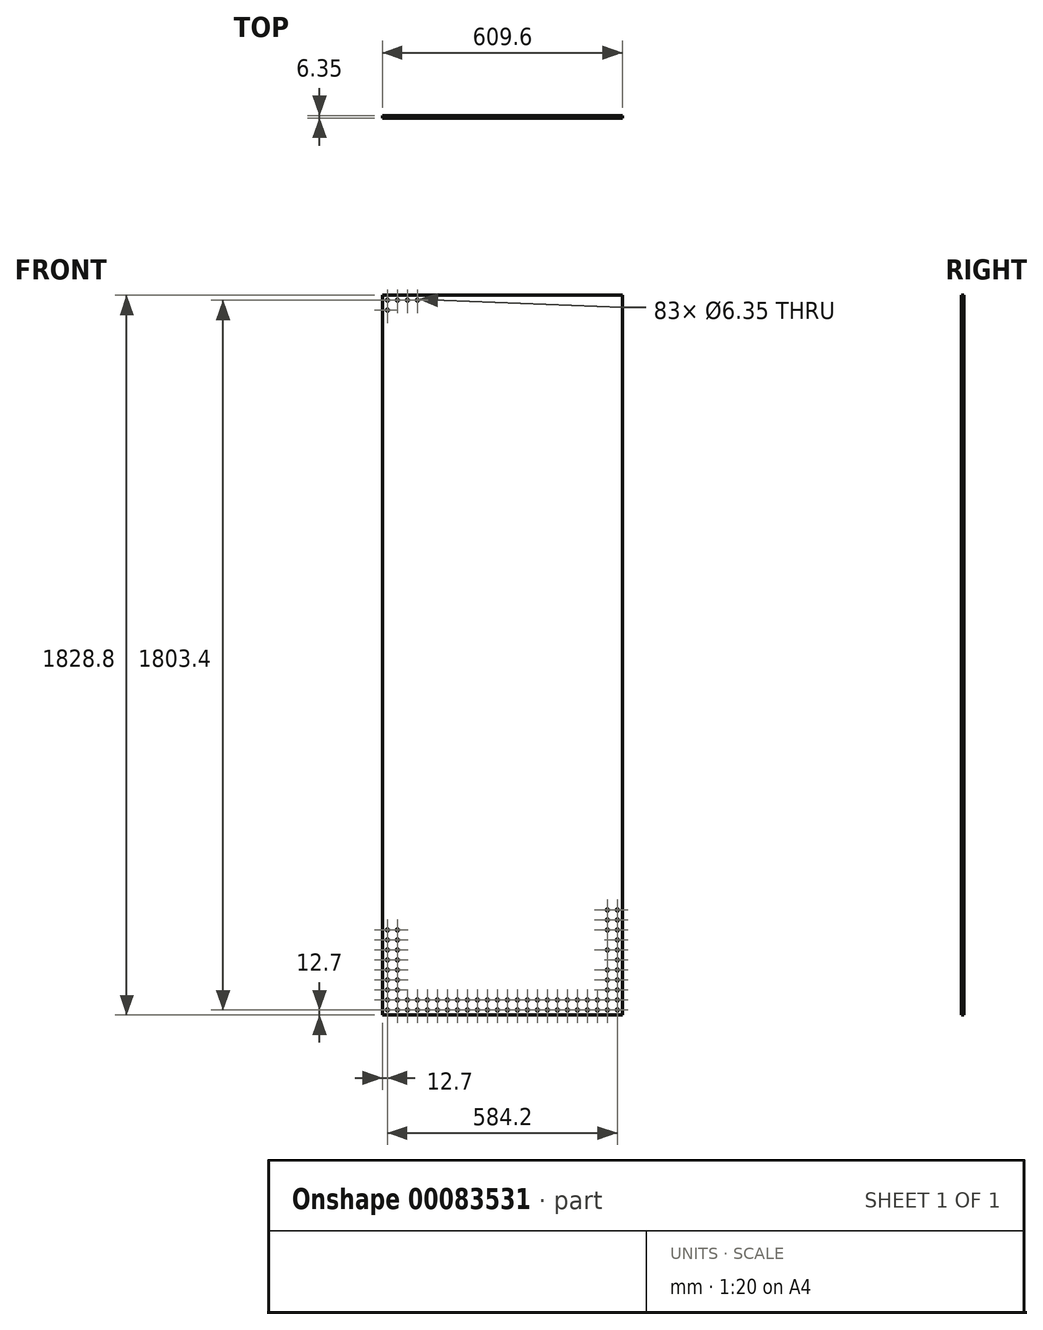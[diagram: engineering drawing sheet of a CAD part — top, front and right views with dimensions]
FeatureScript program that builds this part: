
annotation { "Feature Type Name" : "Feature", "Feature Type Description" : "" }
export const myFeature = defineFeature(function(context is Context, id is Id, definition is map)
    precondition{}
    {
        {
            var Q0;
            Q0=qCreatedBy(makeId("Front.planeOp"),FACE);
            var sketch = newSketch(context, id + "F0", { "sketchPlane" : qUnion([Q0])});
            skLineSegment(sketch, "E0.bottom", {"start": v(-304.8, 914.4) * mm, "end": v(304.8, 914.4) * mm});
            skLineSegment(sketch, "E0.top", {"start": v(-304.8, -914.4) * mm, "end": v(304.8, -914.4) * mm});
            skLineSegment(sketch, "E0.left", {"start": v(-304.8, 914.4) * mm, "end": v(-304.8, -914.4) * mm});
            skLineSegment(sketch, "E0.right", {"start": v(304.8, 914.4) * mm, "end": v(304.8, -914.4) * mm});
            skPoint(sketch, "E0.middle", {"position": v(0, 0) * mm});
            skPoint(sketch, "E1", {"position": v(-292.1, -901.7) * mm});
            skPoint(sketch, "E2.0.1.0", {"position": v(-292.1, -876.3) * mm});
            skPoint(sketch, "E2.0.2.0", {"position": v(-292.1, -850.9) * mm});
            skPoint(sketch, "E2.0.3.0", {"position": v(-292.1, -825.5) * mm});
            skPoint(sketch, "E2.0.4.0", {"position": v(-292.1, -800.1) * mm});
            skPoint(sketch, "E2.0.5.0", {"position": v(-292.1, -774.7) * mm});
            skPoint(sketch, "E2.0.6.0", {"position": v(-292.1, -749.3) * mm});
            skPoint(sketch, "E2.0.7.0", {"position": v(-292.1, -723.9) * mm});
            skPoint(sketch, "E2.0.8.0", {"position": v(-292.1, -698.5) * mm});
            skPoint(sketch, "E2.0.9.0", {"position": v(-292.1, -673.1) * mm});
            skPoint(sketch, "E2.0.10.0", {"position": v(-292.1, -647.7) * mm});
            skPoint(sketch, "E2.0.11.0", {"position": v(-292.1, -622.3) * mm});
            skPoint(sketch, "E2.0.12.0", {"position": v(-292.1, -596.9) * mm});
            skPoint(sketch, "E2.0.13.0", {"position": v(-292.1, -571.5) * mm});
            skPoint(sketch, "E2.0.14.0", {"position": v(-292.1, -546.1) * mm});
            skPoint(sketch, "E2.0.15.0", {"position": v(-292.1, -520.7) * mm});
            skPoint(sketch, "E2.0.16.0", {"position": v(-292.1, -495.3) * mm});
            skPoint(sketch, "E2.0.17.0", {"position": v(-292.1, -469.9) * mm});
            skPoint(sketch, "E2.0.18.0", {"position": v(-292.1, -444.5) * mm});
            skPoint(sketch, "E2.0.19.0", {"position": v(-292.1, -419.1) * mm});
            skPoint(sketch, "E2.0.20.0", {"position": v(-292.1, -393.7) * mm});
            skPoint(sketch, "E2.0.21.0", {"position": v(-292.1, -368.3) * mm});
            skPoint(sketch, "E2.0.22.0", {"position": v(-292.1, -342.9) * mm});
            skPoint(sketch, "E2.0.23.0", {"position": v(-292.1, -317.5) * mm});
            skPoint(sketch, "E2.0.24.0", {"position": v(-292.1, -292.1) * mm});
            skPoint(sketch, "E2.0.25.0", {"position": v(-292.1, -266.7) * mm});
            skPoint(sketch, "E2.0.26.0", {"position": v(-292.1, -241.3) * mm});
            skPoint(sketch, "E2.0.27.0", {"position": v(-292.1, -215.9) * mm});
            skPoint(sketch, "E2.0.28.0", {"position": v(-292.1, -190.5) * mm});
            skPoint(sketch, "E2.0.29.0", {"position": v(-292.1, -165.1) * mm});
            skPoint(sketch, "E2.0.30.0", {"position": v(-292.1, -139.7) * mm});
            skPoint(sketch, "E2.0.31.0", {"position": v(-292.1, -114.3) * mm});
            skPoint(sketch, "E2.0.32.0", {"position": v(-292.1, -88.9) * mm});
            skPoint(sketch, "E2.0.33.0", {"position": v(-292.1, -63.5) * mm});
            skPoint(sketch, "E2.0.34.0", {"position": v(-292.1, -38.1) * mm});
            skPoint(sketch, "E2.0.35.0", {"position": v(-292.1, -12.7) * mm});
            skPoint(sketch, "E2.0.36.0", {"position": v(-292.1, 12.7) * mm});
            skPoint(sketch, "E2.0.37.0", {"position": v(-292.1, 38.1) * mm});
            skPoint(sketch, "E2.0.38.0", {"position": v(-292.1, 63.5) * mm});
            skPoint(sketch, "E2.0.39.0", {"position": v(-292.1, 88.9) * mm});
            skPoint(sketch, "E2.0.40.0", {"position": v(-292.1, 114.3) * mm});
            skPoint(sketch, "E2.0.41.0", {"position": v(-292.1, 139.7) * mm});
            skPoint(sketch, "E2.0.42.0", {"position": v(-292.1, 165.1) * mm});
            skPoint(sketch, "E2.0.43.0", {"position": v(-292.1, 190.5) * mm});
            skPoint(sketch, "E2.0.44.0", {"position": v(-292.1, 215.9) * mm});
            skPoint(sketch, "E2.0.45.0", {"position": v(-292.1, 241.3) * mm});
            skPoint(sketch, "E2.0.46.0", {"position": v(-292.1, 266.7) * mm});
            skPoint(sketch, "E2.0.47.0", {"position": v(-292.1, 292.1) * mm});
            skPoint(sketch, "E2.0.48.0", {"position": v(-292.1, 317.5) * mm});
            skPoint(sketch, "E2.0.49.0", {"position": v(-292.1, 342.9) * mm});
            skPoint(sketch, "E2.0.50.0", {"position": v(-292.1, 368.3) * mm});
            skPoint(sketch, "E2.0.51.0", {"position": v(-292.1, 393.7) * mm});
            skPoint(sketch, "E2.0.52.0", {"position": v(-292.1, 419.1) * mm});
            skPoint(sketch, "E2.0.53.0", {"position": v(-292.1, 444.5) * mm});
            skPoint(sketch, "E2.0.54.0", {"position": v(-292.1, 469.9) * mm});
            skPoint(sketch, "E2.0.55.0", {"position": v(-292.1, 495.3) * mm});
            skPoint(sketch, "E2.0.56.0", {"position": v(-292.1, 520.7) * mm});
            skPoint(sketch, "E2.0.57.0", {"position": v(-292.1, 546.1) * mm});
            skPoint(sketch, "E2.0.58.0", {"position": v(-292.1, 571.5) * mm});
            skPoint(sketch, "E2.0.59.0", {"position": v(-292.1, 596.9) * mm});
            skPoint(sketch, "E2.0.60.0", {"position": v(-292.1, 622.3) * mm});
            skPoint(sketch, "E2.0.61.0", {"position": v(-292.1, 647.7) * mm});
            skPoint(sketch, "E2.0.62.0", {"position": v(-292.1, 673.1) * mm});
            skPoint(sketch, "E2.0.63.0", {"position": v(-292.1, 698.5) * mm});
            skPoint(sketch, "E2.0.64.0", {"position": v(-292.1, 723.9) * mm});
            skPoint(sketch, "E2.0.65.0", {"position": v(-292.1, 749.3) * mm});
            skPoint(sketch, "E2.0.66.0", {"position": v(-292.1, 774.7) * mm});
            skPoint(sketch, "E2.0.67.0", {"position": v(-292.1, 800.1) * mm});
            skPoint(sketch, "E2.0.68.0", {"position": v(-292.1, 825.5) * mm});
            skPoint(sketch, "E2.0.69.0", {"position": v(-292.1, 850.9) * mm});
            skPoint(sketch, "E2.0.70.0", {"position": v(-292.1, 876.3) * mm});
            skPoint(sketch, "E2.0.71.0", {"position": v(-292.1, 901.7) * mm});
            skPoint(sketch, "E2.1.0.0", {"position": v(-266.7, -901.7) * mm});
            skPoint(sketch, "E2.1.1.0", {"position": v(-266.7, -876.3) * mm});
            skPoint(sketch, "E2.1.2.0", {"position": v(-266.7, -850.9) * mm});
            skPoint(sketch, "E2.1.3.0", {"position": v(-266.7, -825.5) * mm});
            skPoint(sketch, "E2.1.4.0", {"position": v(-266.7, -800.1) * mm});
            skPoint(sketch, "E2.1.5.0", {"position": v(-266.7, -774.7) * mm});
            skPoint(sketch, "E2.1.6.0", {"position": v(-266.7, -749.3) * mm});
            skPoint(sketch, "E2.1.7.0", {"position": v(-266.7, -723.9) * mm});
            skPoint(sketch, "E2.1.8.0", {"position": v(-266.7, -698.5) * mm});
            skPoint(sketch, "E2.1.9.0", {"position": v(-266.7, -673.1) * mm});
            skPoint(sketch, "E2.1.10.0", {"position": v(-266.7, -647.7) * mm});
            skPoint(sketch, "E2.1.11.0", {"position": v(-266.7, -622.3) * mm});
            skPoint(sketch, "E2.1.12.0", {"position": v(-266.7, -596.9) * mm});
            skPoint(sketch, "E2.1.13.0", {"position": v(-266.7, -571.5) * mm});
            skPoint(sketch, "E2.1.14.0", {"position": v(-266.7, -546.1) * mm});
            skPoint(sketch, "E2.1.15.0", {"position": v(-266.7, -520.7) * mm});
            skPoint(sketch, "E2.1.16.0", {"position": v(-266.7, -495.3) * mm});
            skPoint(sketch, "E2.1.17.0", {"position": v(-266.7, -469.9) * mm});
            skPoint(sketch, "E2.1.18.0", {"position": v(-266.7, -444.5) * mm});
            skPoint(sketch, "E2.1.19.0", {"position": v(-266.7, -419.1) * mm});
            skPoint(sketch, "E2.1.20.0", {"position": v(-266.7, -393.7) * mm});
            skPoint(sketch, "E2.1.21.0", {"position": v(-266.7, -368.3) * mm});
            skPoint(sketch, "E2.1.22.0", {"position": v(-266.7, -342.9) * mm});
            skPoint(sketch, "E2.1.23.0", {"position": v(-266.7, -317.5) * mm});
            skPoint(sketch, "E2.1.24.0", {"position": v(-266.7, -292.1) * mm});
            skPoint(sketch, "E2.1.25.0", {"position": v(-266.7, -266.7) * mm});
            skPoint(sketch, "E2.1.26.0", {"position": v(-266.7, -241.3) * mm});
            skPoint(sketch, "E2.1.27.0", {"position": v(-266.7, -215.9) * mm});
            skPoint(sketch, "E2.1.28.0", {"position": v(-266.7, -190.5) * mm});
            skPoint(sketch, "E2.1.29.0", {"position": v(-266.7, -165.1) * mm});
            skPoint(sketch, "E2.1.30.0", {"position": v(-266.7, -139.7) * mm});
            skPoint(sketch, "E2.1.31.0", {"position": v(-266.7, -114.3) * mm});
            skPoint(sketch, "E2.1.32.0", {"position": v(-266.7, -88.9) * mm});
            skPoint(sketch, "E2.1.33.0", {"position": v(-266.7, -63.5) * mm});
            skPoint(sketch, "E2.1.34.0", {"position": v(-266.7, -38.1) * mm});
            skPoint(sketch, "E2.1.35.0", {"position": v(-266.7, -12.7) * mm});
            skPoint(sketch, "E2.1.36.0", {"position": v(-266.7, 12.7) * mm});
            skPoint(sketch, "E2.1.37.0", {"position": v(-266.7, 38.1) * mm});
            skPoint(sketch, "E2.1.38.0", {"position": v(-266.7, 63.5) * mm});
            skPoint(sketch, "E2.1.39.0", {"position": v(-266.7, 88.9) * mm});
            skPoint(sketch, "E2.1.40.0", {"position": v(-266.7, 114.3) * mm});
            skPoint(sketch, "E2.1.41.0", {"position": v(-266.7, 139.7) * mm});
            skPoint(sketch, "E2.1.42.0", {"position": v(-266.7, 165.1) * mm});
            skPoint(sketch, "E2.1.43.0", {"position": v(-266.7, 190.5) * mm});
            skPoint(sketch, "E2.1.44.0", {"position": v(-266.7, 215.9) * mm});
            skPoint(sketch, "E2.1.45.0", {"position": v(-266.7, 241.3) * mm});
            skPoint(sketch, "E2.1.46.0", {"position": v(-266.7, 266.7) * mm});
            skPoint(sketch, "E2.1.47.0", {"position": v(-266.7, 292.1) * mm});
            skPoint(sketch, "E2.1.48.0", {"position": v(-266.7, 317.5) * mm});
            skPoint(sketch, "E2.1.49.0", {"position": v(-266.7, 342.9) * mm});
            skPoint(sketch, "E2.1.50.0", {"position": v(-266.7, 368.3) * mm});
            skPoint(sketch, "E2.1.51.0", {"position": v(-266.7, 393.7) * mm});
            skPoint(sketch, "E2.1.52.0", {"position": v(-266.7, 419.1) * mm});
            skPoint(sketch, "E2.1.53.0", {"position": v(-266.7, 444.5) * mm});
            skPoint(sketch, "E2.1.54.0", {"position": v(-266.7, 469.9) * mm});
            skPoint(sketch, "E2.1.55.0", {"position": v(-266.7, 495.3) * mm});
            skPoint(sketch, "E2.1.56.0", {"position": v(-266.7, 520.7) * mm});
            skPoint(sketch, "E2.1.57.0", {"position": v(-266.7, 546.1) * mm});
            skPoint(sketch, "E2.1.58.0", {"position": v(-266.7, 571.5) * mm});
            skPoint(sketch, "E2.1.59.0", {"position": v(-266.7, 596.9) * mm});
            skPoint(sketch, "E2.1.60.0", {"position": v(-266.7, 622.3) * mm});
            skPoint(sketch, "E2.1.61.0", {"position": v(-266.7, 647.7) * mm});
            skPoint(sketch, "E2.1.62.0", {"position": v(-266.7, 673.1) * mm});
            skPoint(sketch, "E2.1.63.0", {"position": v(-266.7, 698.5) * mm});
            skPoint(sketch, "E2.1.64.0", {"position": v(-266.7, 723.9) * mm});
            skPoint(sketch, "E2.1.65.0", {"position": v(-266.7, 749.3) * mm});
            skPoint(sketch, "E2.1.66.0", {"position": v(-266.7, 774.7) * mm});
            skPoint(sketch, "E2.1.67.0", {"position": v(-266.7, 800.1) * mm});
            skPoint(sketch, "E2.1.68.0", {"position": v(-266.7, 825.5) * mm});
            skPoint(sketch, "E2.1.69.0", {"position": v(-266.7, 850.9) * mm});
            skPoint(sketch, "E2.1.70.0", {"position": v(-266.7, 876.3) * mm});
            skPoint(sketch, "E2.1.71.0", {"position": v(-266.7, 901.7) * mm});
            skPoint(sketch, "E2.2.0.0", {"position": v(-241.3, -901.7) * mm});
            skPoint(sketch, "E2.2.1.0", {"position": v(-241.3, -876.3) * mm});
            skPoint(sketch, "E2.2.2.0", {"position": v(-241.3, -850.9) * mm});
            skPoint(sketch, "E2.2.3.0", {"position": v(-241.3, -825.5) * mm});
            skPoint(sketch, "E2.2.4.0", {"position": v(-241.3, -800.1) * mm});
            skPoint(sketch, "E2.2.5.0", {"position": v(-241.3, -774.7) * mm});
            skPoint(sketch, "E2.2.6.0", {"position": v(-241.3, -749.3) * mm});
            skPoint(sketch, "E2.2.7.0", {"position": v(-241.3, -723.9) * mm});
            skPoint(sketch, "E2.2.8.0", {"position": v(-241.3, -698.5) * mm});
            skPoint(sketch, "E2.2.9.0", {"position": v(-241.3, -673.1) * mm});
            skPoint(sketch, "E2.2.10.0", {"position": v(-241.3, -647.7) * mm});
            skPoint(sketch, "E2.2.11.0", {"position": v(-241.3, -622.3) * mm});
            skPoint(sketch, "E2.2.12.0", {"position": v(-241.3, -596.9) * mm});
            skPoint(sketch, "E2.2.13.0", {"position": v(-241.3, -571.5) * mm});
            skPoint(sketch, "E2.2.14.0", {"position": v(-241.3, -546.1) * mm});
            skPoint(sketch, "E2.2.15.0", {"position": v(-241.3, -520.7) * mm});
            skPoint(sketch, "E2.2.16.0", {"position": v(-241.3, -495.3) * mm});
            skPoint(sketch, "E2.2.17.0", {"position": v(-241.3, -469.9) * mm});
            skPoint(sketch, "E2.2.18.0", {"position": v(-241.3, -444.5) * mm});
            skPoint(sketch, "E2.2.19.0", {"position": v(-241.3, -419.1) * mm});
            skPoint(sketch, "E2.2.20.0", {"position": v(-241.3, -393.7) * mm});
            skPoint(sketch, "E2.2.21.0", {"position": v(-241.3, -368.3) * mm});
            skPoint(sketch, "E2.2.22.0", {"position": v(-241.3, -342.9) * mm});
            skPoint(sketch, "E2.2.23.0", {"position": v(-241.3, -317.5) * mm});
            skPoint(sketch, "E2.2.24.0", {"position": v(-241.3, -292.1) * mm});
            skPoint(sketch, "E2.2.25.0", {"position": v(-241.3, -266.7) * mm});
            skPoint(sketch, "E2.2.26.0", {"position": v(-241.3, -241.3) * mm});
            skPoint(sketch, "E2.2.27.0", {"position": v(-241.3, -215.9) * mm});
            skPoint(sketch, "E2.2.28.0", {"position": v(-241.3, -190.5) * mm});
            skPoint(sketch, "E2.2.29.0", {"position": v(-241.3, -165.1) * mm});
            skPoint(sketch, "E2.2.30.0", {"position": v(-241.3, -139.7) * mm});
            skPoint(sketch, "E2.2.31.0", {"position": v(-241.3, -114.3) * mm});
            skPoint(sketch, "E2.2.32.0", {"position": v(-241.3, -88.9) * mm});
            skPoint(sketch, "E2.2.33.0", {"position": v(-241.3, -63.5) * mm});
            skPoint(sketch, "E2.2.34.0", {"position": v(-241.3, -38.1) * mm});
            skPoint(sketch, "E2.2.35.0", {"position": v(-241.3, -12.7) * mm});
            skPoint(sketch, "E2.2.36.0", {"position": v(-241.3, 12.7) * mm});
            skPoint(sketch, "E2.2.37.0", {"position": v(-241.3, 38.1) * mm});
            skPoint(sketch, "E2.2.38.0", {"position": v(-241.3, 63.5) * mm});
            skPoint(sketch, "E2.2.39.0", {"position": v(-241.3, 88.9) * mm});
            skPoint(sketch, "E2.2.40.0", {"position": v(-241.3, 114.3) * mm});
            skPoint(sketch, "E2.2.41.0", {"position": v(-241.3, 139.7) * mm});
            skPoint(sketch, "E2.2.42.0", {"position": v(-241.3, 165.1) * mm});
            skPoint(sketch, "E2.2.43.0", {"position": v(-241.3, 190.5) * mm});
            skPoint(sketch, "E2.2.44.0", {"position": v(-241.3, 215.9) * mm});
            skPoint(sketch, "E2.2.45.0", {"position": v(-241.3, 241.3) * mm});
            skPoint(sketch, "E2.2.46.0", {"position": v(-241.3, 266.7) * mm});
            skPoint(sketch, "E2.2.47.0", {"position": v(-241.3, 292.1) * mm});
            skPoint(sketch, "E2.2.48.0", {"position": v(-241.3, 317.5) * mm});
            skPoint(sketch, "E2.2.49.0", {"position": v(-241.3, 342.9) * mm});
            skPoint(sketch, "E2.2.50.0", {"position": v(-241.3, 368.3) * mm});
            skPoint(sketch, "E2.2.51.0", {"position": v(-241.3, 393.7) * mm});
            skPoint(sketch, "E2.2.52.0", {"position": v(-241.3, 419.1) * mm});
            skPoint(sketch, "E2.2.53.0", {"position": v(-241.3, 444.5) * mm});
            skPoint(sketch, "E2.2.54.0", {"position": v(-241.3, 469.9) * mm});
            skPoint(sketch, "E2.2.55.0", {"position": v(-241.3, 495.3) * mm});
            skPoint(sketch, "E2.2.56.0", {"position": v(-241.3, 520.7) * mm});
            skPoint(sketch, "E2.2.57.0", {"position": v(-241.3, 546.1) * mm});
            skPoint(sketch, "E2.2.58.0", {"position": v(-241.3, 571.5) * mm});
            skPoint(sketch, "E2.2.59.0", {"position": v(-241.3, 596.9) * mm});
            skPoint(sketch, "E2.2.60.0", {"position": v(-241.3, 622.3) * mm});
            skPoint(sketch, "E2.2.61.0", {"position": v(-241.3, 647.7) * mm});
            skPoint(sketch, "E2.2.62.0", {"position": v(-241.3, 673.1) * mm});
            skPoint(sketch, "E2.2.63.0", {"position": v(-241.3, 698.5) * mm});
            skPoint(sketch, "E2.2.64.0", {"position": v(-241.3, 723.9) * mm});
            skPoint(sketch, "E2.2.65.0", {"position": v(-241.3, 749.3) * mm});
            skPoint(sketch, "E2.2.66.0", {"position": v(-241.3, 774.7) * mm});
            skPoint(sketch, "E2.2.67.0", {"position": v(-241.3, 800.1) * mm});
            skPoint(sketch, "E2.2.68.0", {"position": v(-241.3, 825.5) * mm});
            skPoint(sketch, "E2.2.69.0", {"position": v(-241.3, 850.9) * mm});
            skPoint(sketch, "E2.2.70.0", {"position": v(-241.3, 876.3) * mm});
            skPoint(sketch, "E2.2.71.0", {"position": v(-241.3, 901.7) * mm});
            skPoint(sketch, "E2.3.0.0", {"position": v(-215.9, -901.7) * mm});
            skPoint(sketch, "E2.3.1.0", {"position": v(-215.9, -876.3) * mm});
            skPoint(sketch, "E2.3.2.0", {"position": v(-215.9, -850.9) * mm});
            skPoint(sketch, "E2.3.3.0", {"position": v(-215.9, -825.5) * mm});
            skPoint(sketch, "E2.3.4.0", {"position": v(-215.9, -800.1) * mm});
            skPoint(sketch, "E2.3.5.0", {"position": v(-215.9, -774.7) * mm});
            skPoint(sketch, "E2.3.6.0", {"position": v(-215.9, -749.3) * mm});
            skPoint(sketch, "E2.3.7.0", {"position": v(-215.9, -723.9) * mm});
            skPoint(sketch, "E2.3.8.0", {"position": v(-215.9, -698.5) * mm});
            skPoint(sketch, "E2.3.9.0", {"position": v(-215.9, -673.1) * mm});
            skPoint(sketch, "E2.3.10.0", {"position": v(-215.9, -647.7) * mm});
            skPoint(sketch, "E2.3.11.0", {"position": v(-215.9, -622.3) * mm});
            skPoint(sketch, "E2.3.12.0", {"position": v(-215.9, -596.9) * mm});
            skPoint(sketch, "E2.3.13.0", {"position": v(-215.9, -571.5) * mm});
            skPoint(sketch, "E2.3.14.0", {"position": v(-215.9, -546.1) * mm});
            skPoint(sketch, "E2.3.15.0", {"position": v(-215.9, -520.7) * mm});
            skPoint(sketch, "E2.3.16.0", {"position": v(-215.9, -495.3) * mm});
            skPoint(sketch, "E2.3.17.0", {"position": v(-215.9, -469.9) * mm});
            skPoint(sketch, "E2.3.18.0", {"position": v(-215.9, -444.5) * mm});
            skPoint(sketch, "E2.3.19.0", {"position": v(-215.9, -419.1) * mm});
            skPoint(sketch, "E2.3.20.0", {"position": v(-215.9, -393.7) * mm});
            skPoint(sketch, "E2.3.21.0", {"position": v(-215.9, -368.3) * mm});
            skPoint(sketch, "E2.3.22.0", {"position": v(-215.9, -342.9) * mm});
            skPoint(sketch, "E2.3.23.0", {"position": v(-215.9, -317.5) * mm});
            skPoint(sketch, "E2.3.24.0", {"position": v(-215.9, -292.1) * mm});
            skPoint(sketch, "E2.3.25.0", {"position": v(-215.9, -266.7) * mm});
            skPoint(sketch, "E2.3.26.0", {"position": v(-215.9, -241.3) * mm});
            skPoint(sketch, "E2.3.27.0", {"position": v(-215.9, -215.9) * mm});
            skPoint(sketch, "E2.3.28.0", {"position": v(-215.9, -190.5) * mm});
            skPoint(sketch, "E2.3.29.0", {"position": v(-215.9, -165.1) * mm});
            skPoint(sketch, "E2.3.30.0", {"position": v(-215.9, -139.7) * mm});
            skPoint(sketch, "E2.3.31.0", {"position": v(-215.9, -114.3) * mm});
            skPoint(sketch, "E2.3.32.0", {"position": v(-215.9, -88.9) * mm});
            skPoint(sketch, "E2.3.33.0", {"position": v(-215.9, -63.5) * mm});
            skPoint(sketch, "E2.3.34.0", {"position": v(-215.9, -38.1) * mm});
            skPoint(sketch, "E2.3.35.0", {"position": v(-215.9, -12.7) * mm});
            skPoint(sketch, "E2.3.36.0", {"position": v(-215.9, 12.7) * mm});
            skPoint(sketch, "E2.3.37.0", {"position": v(-215.9, 38.1) * mm});
            skPoint(sketch, "E2.3.38.0", {"position": v(-215.9, 63.5) * mm});
            skPoint(sketch, "E2.3.39.0", {"position": v(-215.9, 88.9) * mm});
            skPoint(sketch, "E2.3.40.0", {"position": v(-215.9, 114.3) * mm});
            skPoint(sketch, "E2.3.41.0", {"position": v(-215.9, 139.7) * mm});
            skPoint(sketch, "E2.3.42.0", {"position": v(-215.9, 165.1) * mm});
            skPoint(sketch, "E2.3.43.0", {"position": v(-215.9, 190.5) * mm});
            skPoint(sketch, "E2.3.44.0", {"position": v(-215.9, 215.9) * mm});
            skPoint(sketch, "E2.3.45.0", {"position": v(-215.9, 241.3) * mm});
            skPoint(sketch, "E2.3.46.0", {"position": v(-215.9, 266.7) * mm});
            skPoint(sketch, "E2.3.47.0", {"position": v(-215.9, 292.1) * mm});
            skPoint(sketch, "E2.3.48.0", {"position": v(-215.9, 317.5) * mm});
            skPoint(sketch, "E2.3.49.0", {"position": v(-215.9, 342.9) * mm});
            skPoint(sketch, "E2.3.50.0", {"position": v(-215.9, 368.3) * mm});
            skPoint(sketch, "E2.3.51.0", {"position": v(-215.9, 393.7) * mm});
            skPoint(sketch, "E2.3.52.0", {"position": v(-215.9, 419.1) * mm});
            skPoint(sketch, "E2.3.53.0", {"position": v(-215.9, 444.5) * mm});
            skPoint(sketch, "E2.3.54.0", {"position": v(-215.9, 469.9) * mm});
            skPoint(sketch, "E2.3.55.0", {"position": v(-215.9, 495.3) * mm});
            skPoint(sketch, "E2.3.56.0", {"position": v(-215.9, 520.7) * mm});
            skPoint(sketch, "E2.3.57.0", {"position": v(-215.9, 546.1) * mm});
            skPoint(sketch, "E2.3.58.0", {"position": v(-215.9, 571.5) * mm});
            skPoint(sketch, "E2.3.59.0", {"position": v(-215.9, 596.9) * mm});
            skPoint(sketch, "E2.3.60.0", {"position": v(-215.9, 622.3) * mm});
            skPoint(sketch, "E2.3.61.0", {"position": v(-215.9, 647.7) * mm});
            skPoint(sketch, "E2.3.62.0", {"position": v(-215.9, 673.1) * mm});
            skPoint(sketch, "E2.3.63.0", {"position": v(-215.9, 698.5) * mm});
            skPoint(sketch, "E2.3.64.0", {"position": v(-215.9, 723.9) * mm});
            skPoint(sketch, "E2.3.65.0", {"position": v(-215.9, 749.3) * mm});
            skPoint(sketch, "E2.3.66.0", {"position": v(-215.9, 774.7) * mm});
            skPoint(sketch, "E2.3.67.0", {"position": v(-215.9, 800.1) * mm});
            skPoint(sketch, "E2.3.68.0", {"position": v(-215.9, 825.5) * mm});
            skPoint(sketch, "E2.3.69.0", {"position": v(-215.9, 850.9) * mm});
            skPoint(sketch, "E2.3.70.0", {"position": v(-215.9, 876.3) * mm});
            skPoint(sketch, "E2.3.71.0", {"position": v(-215.9, 901.7) * mm});
            skPoint(sketch, "E2.4.0.0", {"position": v(-190.5, -901.7) * mm});
            skPoint(sketch, "E2.4.1.0", {"position": v(-190.5, -876.3) * mm});
            skPoint(sketch, "E2.4.2.0", {"position": v(-190.5, -850.9) * mm});
            skPoint(sketch, "E2.4.3.0", {"position": v(-190.5, -825.5) * mm});
            skPoint(sketch, "E2.4.4.0", {"position": v(-190.5, -800.1) * mm});
            skPoint(sketch, "E2.4.5.0", {"position": v(-190.5, -774.7) * mm});
            skPoint(sketch, "E2.4.6.0", {"position": v(-190.5, -749.3) * mm});
            skPoint(sketch, "E2.4.7.0", {"position": v(-190.5, -723.9) * mm});
            skPoint(sketch, "E2.4.8.0", {"position": v(-190.5, -698.5) * mm});
            skPoint(sketch, "E2.4.9.0", {"position": v(-190.5, -673.1) * mm});
            skPoint(sketch, "E2.4.10.0", {"position": v(-190.5, -647.7) * mm});
            skPoint(sketch, "E2.4.11.0", {"position": v(-190.5, -622.3) * mm});
            skPoint(sketch, "E2.4.12.0", {"position": v(-190.5, -596.9) * mm});
            skPoint(sketch, "E2.4.13.0", {"position": v(-190.5, -571.5) * mm});
            skPoint(sketch, "E2.4.14.0", {"position": v(-190.5, -546.1) * mm});
            skPoint(sketch, "E2.4.15.0", {"position": v(-190.5, -520.7) * mm});
            skPoint(sketch, "E2.4.16.0", {"position": v(-190.5, -495.3) * mm});
            skPoint(sketch, "E2.4.17.0", {"position": v(-190.5, -469.9) * mm});
            skPoint(sketch, "E2.4.18.0", {"position": v(-190.5, -444.5) * mm});
            skPoint(sketch, "E2.4.19.0", {"position": v(-190.5, -419.1) * mm});
            skPoint(sketch, "E2.4.20.0", {"position": v(-190.5, -393.7) * mm});
            skPoint(sketch, "E2.4.21.0", {"position": v(-190.5, -368.3) * mm});
            skPoint(sketch, "E2.4.22.0", {"position": v(-190.5, -342.9) * mm});
            skPoint(sketch, "E2.4.23.0", {"position": v(-190.5, -317.5) * mm});
            skPoint(sketch, "E2.4.24.0", {"position": v(-190.5, -292.1) * mm});
            skPoint(sketch, "E2.4.25.0", {"position": v(-190.5, -266.7) * mm});
            skPoint(sketch, "E2.4.26.0", {"position": v(-190.5, -241.3) * mm});
            skPoint(sketch, "E2.4.27.0", {"position": v(-190.5, -215.9) * mm});
            skPoint(sketch, "E2.4.28.0", {"position": v(-190.5, -190.5) * mm});
            skPoint(sketch, "E2.4.29.0", {"position": v(-190.5, -165.1) * mm});
            skPoint(sketch, "E2.4.30.0", {"position": v(-190.5, -139.7) * mm});
            skPoint(sketch, "E2.4.31.0", {"position": v(-190.5, -114.3) * mm});
            skPoint(sketch, "E2.4.32.0", {"position": v(-190.5, -88.9) * mm});
            skPoint(sketch, "E2.4.33.0", {"position": v(-190.5, -63.5) * mm});
            skPoint(sketch, "E2.4.34.0", {"position": v(-190.5, -38.1) * mm});
            skPoint(sketch, "E2.4.35.0", {"position": v(-190.5, -12.7) * mm});
            skPoint(sketch, "E2.4.36.0", {"position": v(-190.5, 12.7) * mm});
            skPoint(sketch, "E2.4.37.0", {"position": v(-190.5, 38.1) * mm});
            skPoint(sketch, "E2.4.38.0", {"position": v(-190.5, 63.5) * mm});
            skPoint(sketch, "E2.4.39.0", {"position": v(-190.5, 88.9) * mm});
            skPoint(sketch, "E2.4.40.0", {"position": v(-190.5, 114.3) * mm});
            skPoint(sketch, "E2.4.41.0", {"position": v(-190.5, 139.7) * mm});
            skPoint(sketch, "E2.4.42.0", {"position": v(-190.5, 165.1) * mm});
            skPoint(sketch, "E2.4.43.0", {"position": v(-190.5, 190.5) * mm});
            skPoint(sketch, "E2.4.44.0", {"position": v(-190.5, 215.9) * mm});
            skPoint(sketch, "E2.4.45.0", {"position": v(-190.5, 241.3) * mm});
            skPoint(sketch, "E2.4.46.0", {"position": v(-190.5, 266.7) * mm});
            skPoint(sketch, "E2.4.47.0", {"position": v(-190.5, 292.1) * mm});
            skPoint(sketch, "E2.4.48.0", {"position": v(-190.5, 317.5) * mm});
            skPoint(sketch, "E2.4.49.0", {"position": v(-190.5, 342.9) * mm});
            skPoint(sketch, "E2.4.50.0", {"position": v(-190.5, 368.3) * mm});
            skPoint(sketch, "E2.4.51.0", {"position": v(-190.5, 393.7) * mm});
            skPoint(sketch, "E2.4.52.0", {"position": v(-190.5, 419.1) * mm});
            skPoint(sketch, "E2.4.53.0", {"position": v(-190.5, 444.5) * mm});
            skPoint(sketch, "E2.4.54.0", {"position": v(-190.5, 469.9) * mm});
            skPoint(sketch, "E2.4.55.0", {"position": v(-190.5, 495.3) * mm});
            skPoint(sketch, "E2.4.56.0", {"position": v(-190.5, 520.7) * mm});
            skPoint(sketch, "E2.4.57.0", {"position": v(-190.5, 546.1) * mm});
            skPoint(sketch, "E2.4.58.0", {"position": v(-190.5, 571.5) * mm});
            skPoint(sketch, "E2.4.59.0", {"position": v(-190.5, 596.9) * mm});
            skPoint(sketch, "E2.4.60.0", {"position": v(-190.5, 622.3) * mm});
            skPoint(sketch, "E2.4.61.0", {"position": v(-190.5, 647.7) * mm});
            skPoint(sketch, "E2.4.62.0", {"position": v(-190.5, 673.1) * mm});
            skPoint(sketch, "E2.4.63.0", {"position": v(-190.5, 698.5) * mm});
            skPoint(sketch, "E2.4.64.0", {"position": v(-190.5, 723.9) * mm});
            skPoint(sketch, "E2.4.65.0", {"position": v(-190.5, 749.3) * mm});
            skPoint(sketch, "E2.4.66.0", {"position": v(-190.5, 774.7) * mm});
            skPoint(sketch, "E2.4.67.0", {"position": v(-190.5, 800.1) * mm});
            skPoint(sketch, "E2.4.68.0", {"position": v(-190.5, 825.5) * mm});
            skPoint(sketch, "E2.4.69.0", {"position": v(-190.5, 850.9) * mm});
            skPoint(sketch, "E2.4.70.0", {"position": v(-190.5, 876.3) * mm});
            skPoint(sketch, "E2.4.71.0", {"position": v(-190.5, 901.7) * mm});
            skPoint(sketch, "E2.5.0.0", {"position": v(-165.1, -901.7) * mm});
            skPoint(sketch, "E2.5.1.0", {"position": v(-165.1, -876.3) * mm});
            skPoint(sketch, "E2.5.2.0", {"position": v(-165.1, -850.9) * mm});
            skPoint(sketch, "E2.5.3.0", {"position": v(-165.1, -825.5) * mm});
            skPoint(sketch, "E2.5.4.0", {"position": v(-165.1, -800.1) * mm});
            skPoint(sketch, "E2.5.5.0", {"position": v(-165.1, -774.7) * mm});
            skPoint(sketch, "E2.5.6.0", {"position": v(-165.1, -749.3) * mm});
            skPoint(sketch, "E2.5.7.0", {"position": v(-165.1, -723.9) * mm});
            skPoint(sketch, "E2.5.8.0", {"position": v(-165.1, -698.5) * mm});
            skPoint(sketch, "E2.5.9.0", {"position": v(-165.1, -673.1) * mm});
            skPoint(sketch, "E2.5.10.0", {"position": v(-165.1, -647.7) * mm});
            skPoint(sketch, "E2.5.11.0", {"position": v(-165.1, -622.3) * mm});
            skPoint(sketch, "E2.5.12.0", {"position": v(-165.1, -596.9) * mm});
            skPoint(sketch, "E2.5.13.0", {"position": v(-165.1, -571.5) * mm});
            skPoint(sketch, "E2.5.14.0", {"position": v(-165.1, -546.1) * mm});
            skPoint(sketch, "E2.5.15.0", {"position": v(-165.1, -520.7) * mm});
            skPoint(sketch, "E2.5.16.0", {"position": v(-165.1, -495.3) * mm});
            skPoint(sketch, "E2.5.17.0", {"position": v(-165.1, -469.9) * mm});
            skPoint(sketch, "E2.5.18.0", {"position": v(-165.1, -444.5) * mm});
            skPoint(sketch, "E2.5.19.0", {"position": v(-165.1, -419.1) * mm});
            skPoint(sketch, "E2.5.20.0", {"position": v(-165.1, -393.7) * mm});
            skPoint(sketch, "E2.5.21.0", {"position": v(-165.1, -368.3) * mm});
            skPoint(sketch, "E2.5.22.0", {"position": v(-165.1, -342.9) * mm});
            skPoint(sketch, "E2.5.23.0", {"position": v(-165.1, -317.5) * mm});
            skPoint(sketch, "E2.5.24.0", {"position": v(-165.1, -292.1) * mm});
            skPoint(sketch, "E2.5.25.0", {"position": v(-165.1, -266.7) * mm});
            skPoint(sketch, "E2.5.26.0", {"position": v(-165.1, -241.3) * mm});
            skPoint(sketch, "E2.5.27.0", {"position": v(-165.1, -215.9) * mm});
            skPoint(sketch, "E2.5.28.0", {"position": v(-165.1, -190.5) * mm});
            skPoint(sketch, "E2.5.29.0", {"position": v(-165.1, -165.1) * mm});
            skPoint(sketch, "E2.5.30.0", {"position": v(-165.1, -139.7) * mm});
            skPoint(sketch, "E2.5.31.0", {"position": v(-165.1, -114.3) * mm});
            skPoint(sketch, "E2.5.32.0", {"position": v(-165.1, -88.9) * mm});
            skPoint(sketch, "E2.5.33.0", {"position": v(-165.1, -63.5) * mm});
            skPoint(sketch, "E2.5.34.0", {"position": v(-165.1, -38.1) * mm});
            skPoint(sketch, "E2.5.35.0", {"position": v(-165.1, -12.7) * mm});
            skPoint(sketch, "E2.5.36.0", {"position": v(-165.1, 12.7) * mm});
            skPoint(sketch, "E2.5.37.0", {"position": v(-165.1, 38.1) * mm});
            skPoint(sketch, "E2.5.38.0", {"position": v(-165.1, 63.5) * mm});
            skPoint(sketch, "E2.5.39.0", {"position": v(-165.1, 88.9) * mm});
            skPoint(sketch, "E2.5.40.0", {"position": v(-165.1, 114.3) * mm});
            skPoint(sketch, "E2.5.41.0", {"position": v(-165.1, 139.7) * mm});
            skPoint(sketch, "E2.5.42.0", {"position": v(-165.1, 165.1) * mm});
            skPoint(sketch, "E2.5.43.0", {"position": v(-165.1, 190.5) * mm});
            skPoint(sketch, "E2.5.44.0", {"position": v(-165.1, 215.9) * mm});
            skPoint(sketch, "E2.5.45.0", {"position": v(-165.1, 241.3) * mm});
            skPoint(sketch, "E2.5.46.0", {"position": v(-165.1, 266.7) * mm});
            skPoint(sketch, "E2.5.47.0", {"position": v(-165.1, 292.1) * mm});
            skPoint(sketch, "E2.5.48.0", {"position": v(-165.1, 317.5) * mm});
            skPoint(sketch, "E2.5.49.0", {"position": v(-165.1, 342.9) * mm});
            skPoint(sketch, "E2.5.50.0", {"position": v(-165.1, 368.3) * mm});
            skPoint(sketch, "E2.5.51.0", {"position": v(-165.1, 393.7) * mm});
            skPoint(sketch, "E2.5.52.0", {"position": v(-165.1, 419.1) * mm});
            skPoint(sketch, "E2.5.53.0", {"position": v(-165.1, 444.5) * mm});
            skPoint(sketch, "E2.5.54.0", {"position": v(-165.1, 469.9) * mm});
            skPoint(sketch, "E2.5.55.0", {"position": v(-165.1, 495.3) * mm});
            skPoint(sketch, "E2.5.56.0", {"position": v(-165.1, 520.7) * mm});
            skPoint(sketch, "E2.5.57.0", {"position": v(-165.1, 546.1) * mm});
            skPoint(sketch, "E2.5.58.0", {"position": v(-165.1, 571.5) * mm});
            skPoint(sketch, "E2.5.59.0", {"position": v(-165.1, 596.9) * mm});
            skPoint(sketch, "E2.5.60.0", {"position": v(-165.1, 622.3) * mm});
            skPoint(sketch, "E2.5.61.0", {"position": v(-165.1, 647.7) * mm});
            skPoint(sketch, "E2.5.62.0", {"position": v(-165.1, 673.1) * mm});
            skPoint(sketch, "E2.5.63.0", {"position": v(-165.1, 698.5) * mm});
            skPoint(sketch, "E2.5.64.0", {"position": v(-165.1, 723.9) * mm});
            skPoint(sketch, "E2.5.65.0", {"position": v(-165.1, 749.3) * mm});
            skPoint(sketch, "E2.5.66.0", {"position": v(-165.1, 774.7) * mm});
            skPoint(sketch, "E2.5.67.0", {"position": v(-165.1, 800.1) * mm});
            skPoint(sketch, "E2.5.68.0", {"position": v(-165.1, 825.5) * mm});
            skPoint(sketch, "E2.5.69.0", {"position": v(-165.1, 850.9) * mm});
            skPoint(sketch, "E2.5.70.0", {"position": v(-165.1, 876.3) * mm});
            skPoint(sketch, "E2.5.71.0", {"position": v(-165.1, 901.7) * mm});
            skPoint(sketch, "E2.6.0.0", {"position": v(-139.7, -901.7) * mm});
            skPoint(sketch, "E2.6.1.0", {"position": v(-139.7, -876.3) * mm});
            skPoint(sketch, "E2.6.2.0", {"position": v(-139.7, -850.9) * mm});
            skPoint(sketch, "E2.6.3.0", {"position": v(-139.7, -825.5) * mm});
            skPoint(sketch, "E2.6.4.0", {"position": v(-139.7, -800.1) * mm});
            skPoint(sketch, "E2.6.5.0", {"position": v(-139.7, -774.7) * mm});
            skPoint(sketch, "E2.6.6.0", {"position": v(-139.7, -749.3) * mm});
            skPoint(sketch, "E2.6.7.0", {"position": v(-139.7, -723.9) * mm});
            skPoint(sketch, "E2.6.8.0", {"position": v(-139.7, -698.5) * mm});
            skPoint(sketch, "E2.6.9.0", {"position": v(-139.7, -673.1) * mm});
            skPoint(sketch, "E2.6.10.0", {"position": v(-139.7, -647.7) * mm});
            skPoint(sketch, "E2.6.11.0", {"position": v(-139.7, -622.3) * mm});
            skPoint(sketch, "E2.6.12.0", {"position": v(-139.7, -596.9) * mm});
            skPoint(sketch, "E2.6.13.0", {"position": v(-139.7, -571.5) * mm});
            skPoint(sketch, "E2.6.14.0", {"position": v(-139.7, -546.1) * mm});
            skPoint(sketch, "E2.6.15.0", {"position": v(-139.7, -520.7) * mm});
            skPoint(sketch, "E2.6.16.0", {"position": v(-139.7, -495.3) * mm});
            skPoint(sketch, "E2.6.17.0", {"position": v(-139.7, -469.9) * mm});
            skPoint(sketch, "E2.6.18.0", {"position": v(-139.7, -444.5) * mm});
            skPoint(sketch, "E2.6.19.0", {"position": v(-139.7, -419.1) * mm});
            skPoint(sketch, "E2.6.20.0", {"position": v(-139.7, -393.7) * mm});
            skPoint(sketch, "E2.6.21.0", {"position": v(-139.7, -368.3) * mm});
            skPoint(sketch, "E2.6.22.0", {"position": v(-139.7, -342.9) * mm});
            skPoint(sketch, "E2.6.23.0", {"position": v(-139.7, -317.5) * mm});
            skPoint(sketch, "E2.6.24.0", {"position": v(-139.7, -292.1) * mm});
            skPoint(sketch, "E2.6.25.0", {"position": v(-139.7, -266.7) * mm});
            skPoint(sketch, "E2.6.26.0", {"position": v(-139.7, -241.3) * mm});
            skPoint(sketch, "E2.6.27.0", {"position": v(-139.7, -215.9) * mm});
            skPoint(sketch, "E2.6.28.0", {"position": v(-139.7, -190.5) * mm});
            skPoint(sketch, "E2.6.29.0", {"position": v(-139.7, -165.1) * mm});
            skPoint(sketch, "E2.6.30.0", {"position": v(-139.7, -139.7) * mm});
            skPoint(sketch, "E2.6.31.0", {"position": v(-139.7, -114.3) * mm});
            skPoint(sketch, "E2.6.32.0", {"position": v(-139.7, -88.9) * mm});
            skPoint(sketch, "E2.6.33.0", {"position": v(-139.7, -63.5) * mm});
            skPoint(sketch, "E2.6.34.0", {"position": v(-139.7, -38.1) * mm});
            skPoint(sketch, "E2.6.35.0", {"position": v(-139.7, -12.7) * mm});
            skPoint(sketch, "E2.6.36.0", {"position": v(-139.7, 12.7) * mm});
            skPoint(sketch, "E2.6.37.0", {"position": v(-139.7, 38.1) * mm});
            skPoint(sketch, "E2.6.38.0", {"position": v(-139.7, 63.5) * mm});
            skPoint(sketch, "E2.6.39.0", {"position": v(-139.7, 88.9) * mm});
            skPoint(sketch, "E2.6.40.0", {"position": v(-139.7, 114.3) * mm});
            skPoint(sketch, "E2.6.41.0", {"position": v(-139.7, 139.7) * mm});
            skPoint(sketch, "E2.6.42.0", {"position": v(-139.7, 165.1) * mm});
            skPoint(sketch, "E2.6.43.0", {"position": v(-139.7, 190.5) * mm});
            skPoint(sketch, "E2.6.44.0", {"position": v(-139.7, 215.9) * mm});
            skPoint(sketch, "E2.6.45.0", {"position": v(-139.7, 241.3) * mm});
            skPoint(sketch, "E2.6.46.0", {"position": v(-139.7, 266.7) * mm});
            skPoint(sketch, "E2.6.47.0", {"position": v(-139.7, 292.1) * mm});
            skPoint(sketch, "E2.6.48.0", {"position": v(-139.7, 317.5) * mm});
            skPoint(sketch, "E2.6.49.0", {"position": v(-139.7, 342.9) * mm});
            skPoint(sketch, "E2.6.50.0", {"position": v(-139.7, 368.3) * mm});
            skPoint(sketch, "E2.6.51.0", {"position": v(-139.7, 393.7) * mm});
            skPoint(sketch, "E2.6.52.0", {"position": v(-139.7, 419.1) * mm});
            skPoint(sketch, "E2.6.53.0", {"position": v(-139.7, 444.5) * mm});
            skPoint(sketch, "E2.6.54.0", {"position": v(-139.7, 469.9) * mm});
            skPoint(sketch, "E2.6.55.0", {"position": v(-139.7, 495.3) * mm});
            skPoint(sketch, "E2.6.56.0", {"position": v(-139.7, 520.7) * mm});
            skPoint(sketch, "E2.6.57.0", {"position": v(-139.7, 546.1) * mm});
            skPoint(sketch, "E2.6.58.0", {"position": v(-139.7, 571.5) * mm});
            skPoint(sketch, "E2.6.59.0", {"position": v(-139.7, 596.9) * mm});
            skPoint(sketch, "E2.6.60.0", {"position": v(-139.7, 622.3) * mm});
            skPoint(sketch, "E2.6.61.0", {"position": v(-139.7, 647.7) * mm});
            skPoint(sketch, "E2.6.62.0", {"position": v(-139.7, 673.1) * mm});
            skPoint(sketch, "E2.6.63.0", {"position": v(-139.7, 698.5) * mm});
            skPoint(sketch, "E2.6.64.0", {"position": v(-139.7, 723.9) * mm});
            skPoint(sketch, "E2.6.65.0", {"position": v(-139.7, 749.3) * mm});
            skPoint(sketch, "E2.6.66.0", {"position": v(-139.7, 774.7) * mm});
            skPoint(sketch, "E2.6.67.0", {"position": v(-139.7, 800.1) * mm});
            skPoint(sketch, "E2.6.68.0", {"position": v(-139.7, 825.5) * mm});
            skPoint(sketch, "E2.6.69.0", {"position": v(-139.7, 850.9) * mm});
            skPoint(sketch, "E2.6.70.0", {"position": v(-139.7, 876.3) * mm});
            skPoint(sketch, "E2.6.71.0", {"position": v(-139.7, 901.7) * mm});
            skPoint(sketch, "E2.7.0.0", {"position": v(-114.3, -901.7) * mm});
            skPoint(sketch, "E2.7.1.0", {"position": v(-114.3, -876.3) * mm});
            skPoint(sketch, "E2.7.2.0", {"position": v(-114.3, -850.9) * mm});
            skPoint(sketch, "E2.7.3.0", {"position": v(-114.3, -825.5) * mm});
            skPoint(sketch, "E2.7.4.0", {"position": v(-114.3, -800.1) * mm});
            skPoint(sketch, "E2.7.5.0", {"position": v(-114.3, -774.7) * mm});
            skPoint(sketch, "E2.7.6.0", {"position": v(-114.3, -749.3) * mm});
            skPoint(sketch, "E2.7.7.0", {"position": v(-114.3, -723.9) * mm});
            skPoint(sketch, "E2.7.8.0", {"position": v(-114.3, -698.5) * mm});
            skPoint(sketch, "E2.7.9.0", {"position": v(-114.3, -673.1) * mm});
            skPoint(sketch, "E2.7.10.0", {"position": v(-114.3, -647.7) * mm});
            skPoint(sketch, "E2.7.11.0", {"position": v(-114.3, -622.3) * mm});
            skPoint(sketch, "E2.7.12.0", {"position": v(-114.3, -596.9) * mm});
            skPoint(sketch, "E2.7.13.0", {"position": v(-114.3, -571.5) * mm});
            skPoint(sketch, "E2.7.14.0", {"position": v(-114.3, -546.1) * mm});
            skPoint(sketch, "E2.7.15.0", {"position": v(-114.3, -520.7) * mm});
            skPoint(sketch, "E2.7.16.0", {"position": v(-114.3, -495.3) * mm});
            skPoint(sketch, "E2.7.17.0", {"position": v(-114.3, -469.9) * mm});
            skPoint(sketch, "E2.7.18.0", {"position": v(-114.3, -444.5) * mm});
            skPoint(sketch, "E2.7.19.0", {"position": v(-114.3, -419.1) * mm});
            skPoint(sketch, "E2.7.20.0", {"position": v(-114.3, -393.7) * mm});
            skPoint(sketch, "E2.7.21.0", {"position": v(-114.3, -368.3) * mm});
            skPoint(sketch, "E2.7.22.0", {"position": v(-114.3, -342.9) * mm});
            skPoint(sketch, "E2.7.23.0", {"position": v(-114.3, -317.5) * mm});
            skPoint(sketch, "E2.7.24.0", {"position": v(-114.3, -292.1) * mm});
            skPoint(sketch, "E2.7.25.0", {"position": v(-114.3, -266.7) * mm});
            skPoint(sketch, "E2.7.26.0", {"position": v(-114.3, -241.3) * mm});
            skPoint(sketch, "E2.7.27.0", {"position": v(-114.3, -215.9) * mm});
            skPoint(sketch, "E2.7.28.0", {"position": v(-114.3, -190.5) * mm});
            skPoint(sketch, "E2.7.29.0", {"position": v(-114.3, -165.1) * mm});
            skPoint(sketch, "E2.7.30.0", {"position": v(-114.3, -139.7) * mm});
            skPoint(sketch, "E2.7.31.0", {"position": v(-114.3, -114.3) * mm});
            skPoint(sketch, "E2.7.32.0", {"position": v(-114.3, -88.9) * mm});
            skPoint(sketch, "E2.7.33.0", {"position": v(-114.3, -63.5) * mm});
            skPoint(sketch, "E2.7.34.0", {"position": v(-114.3, -38.1) * mm});
            skPoint(sketch, "E2.7.35.0", {"position": v(-114.3, -12.7) * mm});
            skPoint(sketch, "E2.7.36.0", {"position": v(-114.3, 12.7) * mm});
            skPoint(sketch, "E2.7.37.0", {"position": v(-114.3, 38.1) * mm});
            skPoint(sketch, "E2.7.38.0", {"position": v(-114.3, 63.5) * mm});
            skPoint(sketch, "E2.7.39.0", {"position": v(-114.3, 88.9) * mm});
            skPoint(sketch, "E2.7.40.0", {"position": v(-114.3, 114.3) * mm});
            skPoint(sketch, "E2.7.41.0", {"position": v(-114.3, 139.7) * mm});
            skPoint(sketch, "E2.7.42.0", {"position": v(-114.3, 165.1) * mm});
            skPoint(sketch, "E2.7.43.0", {"position": v(-114.3, 190.5) * mm});
            skPoint(sketch, "E2.7.44.0", {"position": v(-114.3, 215.9) * mm});
            skPoint(sketch, "E2.7.45.0", {"position": v(-114.3, 241.3) * mm});
            skPoint(sketch, "E2.7.46.0", {"position": v(-114.3, 266.7) * mm});
            skPoint(sketch, "E2.7.47.0", {"position": v(-114.3, 292.1) * mm});
            skPoint(sketch, "E2.7.48.0", {"position": v(-114.3, 317.5) * mm});
            skPoint(sketch, "E2.7.49.0", {"position": v(-114.3, 342.9) * mm});
            skPoint(sketch, "E2.7.50.0", {"position": v(-114.3, 368.3) * mm});
            skPoint(sketch, "E2.7.51.0", {"position": v(-114.3, 393.7) * mm});
            skPoint(sketch, "E2.7.52.0", {"position": v(-114.3, 419.1) * mm});
            skPoint(sketch, "E2.7.53.0", {"position": v(-114.3, 444.5) * mm});
            skPoint(sketch, "E2.7.54.0", {"position": v(-114.3, 469.9) * mm});
            skPoint(sketch, "E2.7.55.0", {"position": v(-114.3, 495.3) * mm});
            skPoint(sketch, "E2.7.56.0", {"position": v(-114.3, 520.7) * mm});
            skPoint(sketch, "E2.7.57.0", {"position": v(-114.3, 546.1) * mm});
            skPoint(sketch, "E2.7.58.0", {"position": v(-114.3, 571.5) * mm});
            skPoint(sketch, "E2.7.59.0", {"position": v(-114.3, 596.9) * mm});
            skPoint(sketch, "E2.7.60.0", {"position": v(-114.3, 622.3) * mm});
            skPoint(sketch, "E2.7.61.0", {"position": v(-114.3, 647.7) * mm});
            skPoint(sketch, "E2.7.62.0", {"position": v(-114.3, 673.1) * mm});
            skPoint(sketch, "E2.7.63.0", {"position": v(-114.3, 698.5) * mm});
            skPoint(sketch, "E2.7.64.0", {"position": v(-114.3, 723.9) * mm});
            skPoint(sketch, "E2.7.65.0", {"position": v(-114.3, 749.3) * mm});
            skPoint(sketch, "E2.7.66.0", {"position": v(-114.3, 774.7) * mm});
            skPoint(sketch, "E2.7.67.0", {"position": v(-114.3, 800.1) * mm});
            skPoint(sketch, "E2.7.68.0", {"position": v(-114.3, 825.5) * mm});
            skPoint(sketch, "E2.7.69.0", {"position": v(-114.3, 850.9) * mm});
            skPoint(sketch, "E2.7.70.0", {"position": v(-114.3, 876.3) * mm});
            skPoint(sketch, "E2.7.71.0", {"position": v(-114.3, 901.7) * mm});
            skPoint(sketch, "E2.8.0.0", {"position": v(-88.9, -901.7) * mm});
            skPoint(sketch, "E2.8.1.0", {"position": v(-88.9, -876.3) * mm});
            skPoint(sketch, "E2.8.2.0", {"position": v(-88.9, -850.9) * mm});
            skPoint(sketch, "E2.8.3.0", {"position": v(-88.9, -825.5) * mm});
            skPoint(sketch, "E2.8.4.0", {"position": v(-88.9, -800.1) * mm});
            skPoint(sketch, "E2.8.5.0", {"position": v(-88.9, -774.7) * mm});
            skPoint(sketch, "E2.8.6.0", {"position": v(-88.9, -749.3) * mm});
            skPoint(sketch, "E2.8.7.0", {"position": v(-88.9, -723.9) * mm});
            skPoint(sketch, "E2.8.8.0", {"position": v(-88.9, -698.5) * mm});
            skPoint(sketch, "E2.8.9.0", {"position": v(-88.9, -673.1) * mm});
            skPoint(sketch, "E2.8.10.0", {"position": v(-88.9, -647.7) * mm});
            skPoint(sketch, "E2.8.11.0", {"position": v(-88.9, -622.3) * mm});
            skPoint(sketch, "E2.8.12.0", {"position": v(-88.9, -596.9) * mm});
            skPoint(sketch, "E2.8.13.0", {"position": v(-88.9, -571.5) * mm});
            skPoint(sketch, "E2.8.14.0", {"position": v(-88.9, -546.1) * mm});
            skPoint(sketch, "E2.8.15.0", {"position": v(-88.9, -520.7) * mm});
            skPoint(sketch, "E2.8.16.0", {"position": v(-88.9, -495.3) * mm});
            skPoint(sketch, "E2.8.17.0", {"position": v(-88.9, -469.9) * mm});
            skPoint(sketch, "E2.8.18.0", {"position": v(-88.9, -444.5) * mm});
            skPoint(sketch, "E2.8.19.0", {"position": v(-88.9, -419.1) * mm});
            skPoint(sketch, "E2.8.20.0", {"position": v(-88.9, -393.7) * mm});
            skPoint(sketch, "E2.8.21.0", {"position": v(-88.9, -368.3) * mm});
            skPoint(sketch, "E2.8.22.0", {"position": v(-88.9, -342.9) * mm});
            skPoint(sketch, "E2.8.23.0", {"position": v(-88.9, -317.5) * mm});
            skPoint(sketch, "E2.8.24.0", {"position": v(-88.9, -292.1) * mm});
            skPoint(sketch, "E2.8.25.0", {"position": v(-88.9, -266.7) * mm});
            skPoint(sketch, "E2.8.26.0", {"position": v(-88.9, -241.3) * mm});
            skPoint(sketch, "E2.8.27.0", {"position": v(-88.9, -215.9) * mm});
            skPoint(sketch, "E2.8.28.0", {"position": v(-88.9, -190.5) * mm});
            skPoint(sketch, "E2.8.29.0", {"position": v(-88.9, -165.1) * mm});
            skPoint(sketch, "E2.8.30.0", {"position": v(-88.9, -139.7) * mm});
            skPoint(sketch, "E2.8.31.0", {"position": v(-88.9, -114.3) * mm});
            skPoint(sketch, "E2.8.32.0", {"position": v(-88.9, -88.9) * mm});
            skPoint(sketch, "E2.8.33.0", {"position": v(-88.9, -63.5) * mm});
            skPoint(sketch, "E2.8.34.0", {"position": v(-88.9, -38.1) * mm});
            skPoint(sketch, "E2.8.35.0", {"position": v(-88.9, -12.7) * mm});
            skPoint(sketch, "E2.8.36.0", {"position": v(-88.9, 12.7) * mm});
            skPoint(sketch, "E2.8.37.0", {"position": v(-88.9, 38.1) * mm});
            skPoint(sketch, "E2.8.38.0", {"position": v(-88.9, 63.5) * mm});
            skPoint(sketch, "E2.8.39.0", {"position": v(-88.9, 88.9) * mm});
            skPoint(sketch, "E2.8.40.0", {"position": v(-88.9, 114.3) * mm});
            skPoint(sketch, "E2.8.41.0", {"position": v(-88.9, 139.7) * mm});
            skPoint(sketch, "E2.8.42.0", {"position": v(-88.9, 165.1) * mm});
            skPoint(sketch, "E2.8.43.0", {"position": v(-88.9, 190.5) * mm});
            skPoint(sketch, "E2.8.44.0", {"position": v(-88.9, 215.9) * mm});
            skPoint(sketch, "E2.8.45.0", {"position": v(-88.9, 241.3) * mm});
            skPoint(sketch, "E2.8.46.0", {"position": v(-88.9, 266.7) * mm});
            skPoint(sketch, "E2.8.47.0", {"position": v(-88.9, 292.1) * mm});
            skPoint(sketch, "E2.8.48.0", {"position": v(-88.9, 317.5) * mm});
            skPoint(sketch, "E2.8.49.0", {"position": v(-88.9, 342.9) * mm});
            skPoint(sketch, "E2.8.50.0", {"position": v(-88.9, 368.3) * mm});
            skPoint(sketch, "E2.8.51.0", {"position": v(-88.9, 393.7) * mm});
            skPoint(sketch, "E2.8.52.0", {"position": v(-88.9, 419.1) * mm});
            skPoint(sketch, "E2.8.53.0", {"position": v(-88.9, 444.5) * mm});
            skPoint(sketch, "E2.8.54.0", {"position": v(-88.9, 469.9) * mm});
            skPoint(sketch, "E2.8.55.0", {"position": v(-88.9, 495.3) * mm});
            skPoint(sketch, "E2.8.56.0", {"position": v(-88.9, 520.7) * mm});
            skPoint(sketch, "E2.8.57.0", {"position": v(-88.9, 546.1) * mm});
            skPoint(sketch, "E2.8.58.0", {"position": v(-88.9, 571.5) * mm});
            skPoint(sketch, "E2.8.59.0", {"position": v(-88.9, 596.9) * mm});
            skPoint(sketch, "E2.8.60.0", {"position": v(-88.9, 622.3) * mm});
            skPoint(sketch, "E2.8.61.0", {"position": v(-88.9, 647.7) * mm});
            skPoint(sketch, "E2.8.62.0", {"position": v(-88.9, 673.1) * mm});
            skPoint(sketch, "E2.8.63.0", {"position": v(-88.9, 698.5) * mm});
            skPoint(sketch, "E2.8.64.0", {"position": v(-88.9, 723.9) * mm});
            skPoint(sketch, "E2.8.65.0", {"position": v(-88.9, 749.3) * mm});
            skPoint(sketch, "E2.8.66.0", {"position": v(-88.9, 774.7) * mm});
            skPoint(sketch, "E2.8.67.0", {"position": v(-88.9, 800.1) * mm});
            skPoint(sketch, "E2.8.68.0", {"position": v(-88.9, 825.5) * mm});
            skPoint(sketch, "E2.8.69.0", {"position": v(-88.9, 850.9) * mm});
            skPoint(sketch, "E2.8.70.0", {"position": v(-88.9, 876.3) * mm});
            skPoint(sketch, "E2.8.71.0", {"position": v(-88.9, 901.7) * mm});
            skPoint(sketch, "E2.9.0.0", {"position": v(-63.5, -901.7) * mm});
            skPoint(sketch, "E2.9.1.0", {"position": v(-63.5, -876.3) * mm});
            skPoint(sketch, "E2.9.2.0", {"position": v(-63.5, -850.9) * mm});
            skPoint(sketch, "E2.9.3.0", {"position": v(-63.5, -825.5) * mm});
            skPoint(sketch, "E2.9.4.0", {"position": v(-63.5, -800.1) * mm});
            skPoint(sketch, "E2.9.5.0", {"position": v(-63.5, -774.7) * mm});
            skPoint(sketch, "E2.9.6.0", {"position": v(-63.5, -749.3) * mm});
            skPoint(sketch, "E2.9.7.0", {"position": v(-63.5, -723.9) * mm});
            skPoint(sketch, "E2.9.8.0", {"position": v(-63.5, -698.5) * mm});
            skPoint(sketch, "E2.9.9.0", {"position": v(-63.5, -673.1) * mm});
            skPoint(sketch, "E2.9.10.0", {"position": v(-63.5, -647.7) * mm});
            skPoint(sketch, "E2.9.11.0", {"position": v(-63.5, -622.3) * mm});
            skPoint(sketch, "E2.9.12.0", {"position": v(-63.5, -596.9) * mm});
            skPoint(sketch, "E2.9.13.0", {"position": v(-63.5, -571.5) * mm});
            skPoint(sketch, "E2.9.14.0", {"position": v(-63.5, -546.1) * mm});
            skPoint(sketch, "E2.9.15.0", {"position": v(-63.5, -520.7) * mm});
            skPoint(sketch, "E2.9.16.0", {"position": v(-63.5, -495.3) * mm});
            skPoint(sketch, "E2.9.17.0", {"position": v(-63.5, -469.9) * mm});
            skPoint(sketch, "E2.9.18.0", {"position": v(-63.5, -444.5) * mm});
            skPoint(sketch, "E2.9.19.0", {"position": v(-63.5, -419.1) * mm});
            skPoint(sketch, "E2.9.20.0", {"position": v(-63.5, -393.7) * mm});
            skPoint(sketch, "E2.9.21.0", {"position": v(-63.5, -368.3) * mm});
            skPoint(sketch, "E2.9.22.0", {"position": v(-63.5, -342.9) * mm});
            skPoint(sketch, "E2.9.23.0", {"position": v(-63.5, -317.5) * mm});
            skPoint(sketch, "E2.9.24.0", {"position": v(-63.5, -292.1) * mm});
            skPoint(sketch, "E2.9.25.0", {"position": v(-63.5, -266.7) * mm});
            skPoint(sketch, "E2.9.26.0", {"position": v(-63.5, -241.3) * mm});
            skPoint(sketch, "E2.9.27.0", {"position": v(-63.5, -215.9) * mm});
            skPoint(sketch, "E2.9.28.0", {"position": v(-63.5, -190.5) * mm});
            skPoint(sketch, "E2.9.29.0", {"position": v(-63.5, -165.1) * mm});
            skPoint(sketch, "E2.9.30.0", {"position": v(-63.5, -139.7) * mm});
            skPoint(sketch, "E2.9.31.0", {"position": v(-63.5, -114.3) * mm});
            skPoint(sketch, "E2.9.32.0", {"position": v(-63.5, -88.9) * mm});
            skPoint(sketch, "E2.9.33.0", {"position": v(-63.5, -63.5) * mm});
            skPoint(sketch, "E2.9.34.0", {"position": v(-63.5, -38.1) * mm});
            skPoint(sketch, "E2.9.35.0", {"position": v(-63.5, -12.7) * mm});
            skPoint(sketch, "E2.9.36.0", {"position": v(-63.5, 12.7) * mm});
            skPoint(sketch, "E2.9.37.0", {"position": v(-63.5, 38.1) * mm});
            skPoint(sketch, "E2.9.38.0", {"position": v(-63.5, 63.5) * mm});
            skPoint(sketch, "E2.9.39.0", {"position": v(-63.5, 88.9) * mm});
            skPoint(sketch, "E2.9.40.0", {"position": v(-63.5, 114.3) * mm});
            skPoint(sketch, "E2.9.41.0", {"position": v(-63.5, 139.7) * mm});
            skPoint(sketch, "E2.9.42.0", {"position": v(-63.5, 165.1) * mm});
            skPoint(sketch, "E2.9.43.0", {"position": v(-63.5, 190.5) * mm});
            skPoint(sketch, "E2.9.44.0", {"position": v(-63.5, 215.9) * mm});
            skPoint(sketch, "E2.9.45.0", {"position": v(-63.5, 241.3) * mm});
            skPoint(sketch, "E2.9.46.0", {"position": v(-63.5, 266.7) * mm});
            skPoint(sketch, "E2.9.47.0", {"position": v(-63.5, 292.1) * mm});
            skPoint(sketch, "E2.9.48.0", {"position": v(-63.5, 317.5) * mm});
            skPoint(sketch, "E2.9.49.0", {"position": v(-63.5, 342.9) * mm});
            skPoint(sketch, "E2.9.50.0", {"position": v(-63.5, 368.3) * mm});
            skPoint(sketch, "E2.9.51.0", {"position": v(-63.5, 393.7) * mm});
            skPoint(sketch, "E2.9.52.0", {"position": v(-63.5, 419.1) * mm});
            skPoint(sketch, "E2.9.53.0", {"position": v(-63.5, 444.5) * mm});
            skPoint(sketch, "E2.9.54.0", {"position": v(-63.5, 469.9) * mm});
            skPoint(sketch, "E2.9.55.0", {"position": v(-63.5, 495.3) * mm});
            skPoint(sketch, "E2.9.56.0", {"position": v(-63.5, 520.7) * mm});
            skPoint(sketch, "E2.9.57.0", {"position": v(-63.5, 546.1) * mm});
            skPoint(sketch, "E2.9.58.0", {"position": v(-63.5, 571.5) * mm});
            skPoint(sketch, "E2.9.59.0", {"position": v(-63.5, 596.9) * mm});
            skPoint(sketch, "E2.9.60.0", {"position": v(-63.5, 622.3) * mm});
            skPoint(sketch, "E2.9.61.0", {"position": v(-63.5, 647.7) * mm});
            skPoint(sketch, "E2.9.62.0", {"position": v(-63.5, 673.1) * mm});
            skPoint(sketch, "E2.9.63.0", {"position": v(-63.5, 698.5) * mm});
            skPoint(sketch, "E2.9.64.0", {"position": v(-63.5, 723.9) * mm});
            skPoint(sketch, "E2.9.65.0", {"position": v(-63.5, 749.3) * mm});
            skPoint(sketch, "E2.9.66.0", {"position": v(-63.5, 774.7) * mm});
            skPoint(sketch, "E2.9.67.0", {"position": v(-63.5, 800.1) * mm});
            skPoint(sketch, "E2.9.68.0", {"position": v(-63.5, 825.5) * mm});
            skPoint(sketch, "E2.9.69.0", {"position": v(-63.5, 850.9) * mm});
            skPoint(sketch, "E2.9.70.0", {"position": v(-63.5, 876.3) * mm});
            skPoint(sketch, "E2.9.71.0", {"position": v(-63.5, 901.7) * mm});
            skPoint(sketch, "E2.10.0.0", {"position": v(-38.1, -901.7) * mm});
            skPoint(sketch, "E2.10.1.0", {"position": v(-38.1, -876.3) * mm});
            skPoint(sketch, "E2.10.2.0", {"position": v(-38.1, -850.9) * mm});
            skPoint(sketch, "E2.10.3.0", {"position": v(-38.1, -825.5) * mm});
            skPoint(sketch, "E2.10.4.0", {"position": v(-38.1, -800.1) * mm});
            skPoint(sketch, "E2.10.5.0", {"position": v(-38.1, -774.7) * mm});
            skPoint(sketch, "E2.10.6.0", {"position": v(-38.1, -749.3) * mm});
            skPoint(sketch, "E2.10.7.0", {"position": v(-38.1, -723.9) * mm});
            skPoint(sketch, "E2.10.8.0", {"position": v(-38.1, -698.5) * mm});
            skPoint(sketch, "E2.10.9.0", {"position": v(-38.1, -673.1) * mm});
            skPoint(sketch, "E2.10.10.0", {"position": v(-38.1, -647.7) * mm});
            skPoint(sketch, "E2.10.11.0", {"position": v(-38.1, -622.3) * mm});
            skPoint(sketch, "E2.10.12.0", {"position": v(-38.1, -596.9) * mm});
            skPoint(sketch, "E2.10.13.0", {"position": v(-38.1, -571.5) * mm});
            skPoint(sketch, "E2.10.14.0", {"position": v(-38.1, -546.1) * mm});
            skPoint(sketch, "E2.10.15.0", {"position": v(-38.1, -520.7) * mm});
            skPoint(sketch, "E2.10.16.0", {"position": v(-38.1, -495.3) * mm});
            skPoint(sketch, "E2.10.17.0", {"position": v(-38.1, -469.9) * mm});
            skPoint(sketch, "E2.10.18.0", {"position": v(-38.1, -444.5) * mm});
            skPoint(sketch, "E2.10.19.0", {"position": v(-38.1, -419.1) * mm});
            skPoint(sketch, "E2.10.20.0", {"position": v(-38.1, -393.7) * mm});
            skPoint(sketch, "E2.10.21.0", {"position": v(-38.1, -368.3) * mm});
            skPoint(sketch, "E2.10.22.0", {"position": v(-38.1, -342.9) * mm});
            skPoint(sketch, "E2.10.23.0", {"position": v(-38.1, -317.5) * mm});
            skPoint(sketch, "E2.10.24.0", {"position": v(-38.1, -292.1) * mm});
            skPoint(sketch, "E2.10.25.0", {"position": v(-38.1, -266.7) * mm});
            skPoint(sketch, "E2.10.26.0", {"position": v(-38.1, -241.3) * mm});
            skPoint(sketch, "E2.10.27.0", {"position": v(-38.1, -215.9) * mm});
            skPoint(sketch, "E2.10.28.0", {"position": v(-38.1, -190.5) * mm});
            skPoint(sketch, "E2.10.29.0", {"position": v(-38.1, -165.1) * mm});
            skPoint(sketch, "E2.10.30.0", {"position": v(-38.1, -139.7) * mm});
            skPoint(sketch, "E2.10.31.0", {"position": v(-38.1, -114.3) * mm});
            skPoint(sketch, "E2.10.32.0", {"position": v(-38.1, -88.9) * mm});
            skPoint(sketch, "E2.10.33.0", {"position": v(-38.1, -63.5) * mm});
            skPoint(sketch, "E2.10.34.0", {"position": v(-38.1, -38.1) * mm});
            skPoint(sketch, "E2.10.35.0", {"position": v(-38.1, -12.7) * mm});
            skPoint(sketch, "E2.10.36.0", {"position": v(-38.1, 12.7) * mm});
            skPoint(sketch, "E2.10.37.0", {"position": v(-38.1, 38.1) * mm});
            skPoint(sketch, "E2.10.38.0", {"position": v(-38.1, 63.5) * mm});
            skPoint(sketch, "E2.10.39.0", {"position": v(-38.1, 88.9) * mm});
            skPoint(sketch, "E2.10.40.0", {"position": v(-38.1, 114.3) * mm});
            skPoint(sketch, "E2.10.41.0", {"position": v(-38.1, 139.7) * mm});
            skPoint(sketch, "E2.10.42.0", {"position": v(-38.1, 165.1) * mm});
            skPoint(sketch, "E2.10.43.0", {"position": v(-38.1, 190.5) * mm});
            skPoint(sketch, "E2.10.44.0", {"position": v(-38.1, 215.9) * mm});
            skPoint(sketch, "E2.10.45.0", {"position": v(-38.1, 241.3) * mm});
            skPoint(sketch, "E2.10.46.0", {"position": v(-38.1, 266.7) * mm});
            skPoint(sketch, "E2.10.47.0", {"position": v(-38.1, 292.1) * mm});
            skPoint(sketch, "E2.10.48.0", {"position": v(-38.1, 317.5) * mm});
            skPoint(sketch, "E2.10.49.0", {"position": v(-38.1, 342.9) * mm});
            skPoint(sketch, "E2.10.50.0", {"position": v(-38.1, 368.3) * mm});
            skPoint(sketch, "E2.10.51.0", {"position": v(-38.1, 393.7) * mm});
            skPoint(sketch, "E2.10.52.0", {"position": v(-38.1, 419.1) * mm});
            skPoint(sketch, "E2.10.53.0", {"position": v(-38.1, 444.5) * mm});
            skPoint(sketch, "E2.10.54.0", {"position": v(-38.1, 469.9) * mm});
            skPoint(sketch, "E2.10.55.0", {"position": v(-38.1, 495.3) * mm});
            skPoint(sketch, "E2.10.56.0", {"position": v(-38.1, 520.7) * mm});
            skPoint(sketch, "E2.10.57.0", {"position": v(-38.1, 546.1) * mm});
            skPoint(sketch, "E2.10.58.0", {"position": v(-38.1, 571.5) * mm});
            skPoint(sketch, "E2.10.59.0", {"position": v(-38.1, 596.9) * mm});
            skPoint(sketch, "E2.10.60.0", {"position": v(-38.1, 622.3) * mm});
            skPoint(sketch, "E2.10.61.0", {"position": v(-38.1, 647.7) * mm});
            skPoint(sketch, "E2.10.62.0", {"position": v(-38.1, 673.1) * mm});
            skPoint(sketch, "E2.10.63.0", {"position": v(-38.1, 698.5) * mm});
            skPoint(sketch, "E2.10.64.0", {"position": v(-38.1, 723.9) * mm});
            skPoint(sketch, "E2.10.65.0", {"position": v(-38.1, 749.3) * mm});
            skPoint(sketch, "E2.10.66.0", {"position": v(-38.1, 774.7) * mm});
            skPoint(sketch, "E2.10.67.0", {"position": v(-38.1, 800.1) * mm});
            skPoint(sketch, "E2.10.68.0", {"position": v(-38.1, 825.5) * mm});
            skPoint(sketch, "E2.10.69.0", {"position": v(-38.1, 850.9) * mm});
            skPoint(sketch, "E2.10.70.0", {"position": v(-38.1, 876.3) * mm});
            skPoint(sketch, "E2.10.71.0", {"position": v(-38.1, 901.7) * mm});
            skPoint(sketch, "E2.11.0.0", {"position": v(-12.7, -901.7) * mm});
            skPoint(sketch, "E2.11.1.0", {"position": v(-12.7, -876.3) * mm});
            skPoint(sketch, "E2.11.2.0", {"position": v(-12.7, -850.9) * mm});
            skPoint(sketch, "E2.11.3.0", {"position": v(-12.7, -825.5) * mm});
            skPoint(sketch, "E2.11.4.0", {"position": v(-12.7, -800.1) * mm});
            skPoint(sketch, "E2.11.5.0", {"position": v(-12.7, -774.7) * mm});
            skPoint(sketch, "E2.11.6.0", {"position": v(-12.7, -749.3) * mm});
            skPoint(sketch, "E2.11.7.0", {"position": v(-12.7, -723.9) * mm});
            skPoint(sketch, "E2.11.8.0", {"position": v(-12.7, -698.5) * mm});
            skPoint(sketch, "E2.11.9.0", {"position": v(-12.7, -673.1) * mm});
            skPoint(sketch, "E2.11.10.0", {"position": v(-12.7, -647.7) * mm});
            skPoint(sketch, "E2.11.11.0", {"position": v(-12.7, -622.3) * mm});
            skPoint(sketch, "E2.11.12.0", {"position": v(-12.7, -596.9) * mm});
            skPoint(sketch, "E2.11.13.0", {"position": v(-12.7, -571.5) * mm});
            skPoint(sketch, "E2.11.14.0", {"position": v(-12.7, -546.1) * mm});
            skPoint(sketch, "E2.11.15.0", {"position": v(-12.7, -520.7) * mm});
            skPoint(sketch, "E2.11.16.0", {"position": v(-12.7, -495.3) * mm});
            skPoint(sketch, "E2.11.17.0", {"position": v(-12.7, -469.9) * mm});
            skPoint(sketch, "E2.11.18.0", {"position": v(-12.7, -444.5) * mm});
            skPoint(sketch, "E2.11.19.0", {"position": v(-12.7, -419.1) * mm});
            skPoint(sketch, "E2.11.20.0", {"position": v(-12.7, -393.7) * mm});
            skPoint(sketch, "E2.11.21.0", {"position": v(-12.7, -368.3) * mm});
            skPoint(sketch, "E2.11.22.0", {"position": v(-12.7, -342.9) * mm});
            skPoint(sketch, "E2.11.23.0", {"position": v(-12.7, -317.5) * mm});
            skPoint(sketch, "E2.11.24.0", {"position": v(-12.7, -292.1) * mm});
            skPoint(sketch, "E2.11.25.0", {"position": v(-12.7, -266.7) * mm});
            skPoint(sketch, "E2.11.26.0", {"position": v(-12.7, -241.3) * mm});
            skPoint(sketch, "E2.11.27.0", {"position": v(-12.7, -215.9) * mm});
            skPoint(sketch, "E2.11.28.0", {"position": v(-12.7, -190.5) * mm});
            skPoint(sketch, "E2.11.29.0", {"position": v(-12.7, -165.1) * mm});
            skPoint(sketch, "E2.11.30.0", {"position": v(-12.7, -139.7) * mm});
            skPoint(sketch, "E2.11.31.0", {"position": v(-12.7, -114.3) * mm});
            skPoint(sketch, "E2.11.32.0", {"position": v(-12.7, -88.9) * mm});
            skPoint(sketch, "E2.11.33.0", {"position": v(-12.7, -63.5) * mm});
            skPoint(sketch, "E2.11.34.0", {"position": v(-12.7, -38.1) * mm});
            skPoint(sketch, "E2.11.35.0", {"position": v(-12.7, -12.7) * mm});
            skPoint(sketch, "E2.11.36.0", {"position": v(-12.7, 12.7) * mm});
            skPoint(sketch, "E2.11.37.0", {"position": v(-12.7, 38.1) * mm});
            skPoint(sketch, "E2.11.38.0", {"position": v(-12.7, 63.5) * mm});
            skPoint(sketch, "E2.11.39.0", {"position": v(-12.7, 88.9) * mm});
            skPoint(sketch, "E2.11.40.0", {"position": v(-12.7, 114.3) * mm});
            skPoint(sketch, "E2.11.41.0", {"position": v(-12.7, 139.7) * mm});
            skPoint(sketch, "E2.11.42.0", {"position": v(-12.7, 165.1) * mm});
            skPoint(sketch, "E2.11.43.0", {"position": v(-12.7, 190.5) * mm});
            skPoint(sketch, "E2.11.44.0", {"position": v(-12.7, 215.9) * mm});
            skPoint(sketch, "E2.11.45.0", {"position": v(-12.7, 241.3) * mm});
            skPoint(sketch, "E2.11.46.0", {"position": v(-12.7, 266.7) * mm});
            skPoint(sketch, "E2.11.47.0", {"position": v(-12.7, 292.1) * mm});
            skPoint(sketch, "E2.11.48.0", {"position": v(-12.7, 317.5) * mm});
            skPoint(sketch, "E2.11.49.0", {"position": v(-12.7, 342.9) * mm});
            skPoint(sketch, "E2.11.50.0", {"position": v(-12.7, 368.3) * mm});
            skPoint(sketch, "E2.11.51.0", {"position": v(-12.7, 393.7) * mm});
            skPoint(sketch, "E2.11.52.0", {"position": v(-12.7, 419.1) * mm});
            skPoint(sketch, "E2.11.53.0", {"position": v(-12.7, 444.5) * mm});
            skPoint(sketch, "E2.11.54.0", {"position": v(-12.7, 469.9) * mm});
            skPoint(sketch, "E2.11.55.0", {"position": v(-12.7, 495.3) * mm});
            skPoint(sketch, "E2.11.56.0", {"position": v(-12.7, 520.7) * mm});
            skPoint(sketch, "E2.11.57.0", {"position": v(-12.7, 546.1) * mm});
            skPoint(sketch, "E2.11.58.0", {"position": v(-12.7, 571.5) * mm});
            skPoint(sketch, "E2.11.59.0", {"position": v(-12.7, 596.9) * mm});
            skPoint(sketch, "E2.11.60.0", {"position": v(-12.7, 622.3) * mm});
            skPoint(sketch, "E2.11.61.0", {"position": v(-12.7, 647.7) * mm});
            skPoint(sketch, "E2.11.62.0", {"position": v(-12.7, 673.1) * mm});
            skPoint(sketch, "E2.11.63.0", {"position": v(-12.7, 698.5) * mm});
            skPoint(sketch, "E2.11.64.0", {"position": v(-12.7, 723.9) * mm});
            skPoint(sketch, "E2.11.65.0", {"position": v(-12.7, 749.3) * mm});
            skPoint(sketch, "E2.11.66.0", {"position": v(-12.7, 774.7) * mm});
            skPoint(sketch, "E2.11.67.0", {"position": v(-12.7, 800.1) * mm});
            skPoint(sketch, "E2.11.68.0", {"position": v(-12.7, 825.5) * mm});
            skPoint(sketch, "E2.11.69.0", {"position": v(-12.7, 850.9) * mm});
            skPoint(sketch, "E2.11.70.0", {"position": v(-12.7, 876.3) * mm});
            skPoint(sketch, "E2.11.71.0", {"position": v(-12.7, 901.7) * mm});
            skPoint(sketch, "E2.12.0.0", {"position": v(12.7, -901.7) * mm});
            skPoint(sketch, "E2.12.1.0", {"position": v(12.7, -876.3) * mm});
            skPoint(sketch, "E2.12.2.0", {"position": v(12.7, -850.9) * mm});
            skPoint(sketch, "E2.12.3.0", {"position": v(12.7, -825.5) * mm});
            skPoint(sketch, "E2.12.4.0", {"position": v(12.7, -800.1) * mm});
            skPoint(sketch, "E2.12.5.0", {"position": v(12.7, -774.7) * mm});
            skPoint(sketch, "E2.12.6.0", {"position": v(12.7, -749.3) * mm});
            skPoint(sketch, "E2.12.7.0", {"position": v(12.7, -723.9) * mm});
            skPoint(sketch, "E2.12.8.0", {"position": v(12.7, -698.5) * mm});
            skPoint(sketch, "E2.12.9.0", {"position": v(12.7, -673.1) * mm});
            skPoint(sketch, "E2.12.10.0", {"position": v(12.7, -647.7) * mm});
            skPoint(sketch, "E2.12.11.0", {"position": v(12.7, -622.3) * mm});
            skPoint(sketch, "E2.12.12.0", {"position": v(12.7, -596.9) * mm});
            skPoint(sketch, "E2.12.13.0", {"position": v(12.7, -571.5) * mm});
            skPoint(sketch, "E2.12.14.0", {"position": v(12.7, -546.1) * mm});
            skPoint(sketch, "E2.12.15.0", {"position": v(12.7, -520.7) * mm});
            skPoint(sketch, "E2.12.16.0", {"position": v(12.7, -495.3) * mm});
            skPoint(sketch, "E2.12.17.0", {"position": v(12.7, -469.9) * mm});
            skPoint(sketch, "E2.12.18.0", {"position": v(12.7, -444.5) * mm});
            skPoint(sketch, "E2.12.19.0", {"position": v(12.7, -419.1) * mm});
            skPoint(sketch, "E2.12.20.0", {"position": v(12.7, -393.7) * mm});
            skPoint(sketch, "E2.12.21.0", {"position": v(12.7, -368.3) * mm});
            skPoint(sketch, "E2.12.22.0", {"position": v(12.7, -342.9) * mm});
            skPoint(sketch, "E2.12.23.0", {"position": v(12.7, -317.5) * mm});
            skPoint(sketch, "E2.12.24.0", {"position": v(12.7, -292.1) * mm});
            skPoint(sketch, "E2.12.25.0", {"position": v(12.7, -266.7) * mm});
            skPoint(sketch, "E2.12.26.0", {"position": v(12.7, -241.3) * mm});
            skPoint(sketch, "E2.12.27.0", {"position": v(12.7, -215.9) * mm});
            skPoint(sketch, "E2.12.28.0", {"position": v(12.7, -190.5) * mm});
            skPoint(sketch, "E2.12.29.0", {"position": v(12.7, -165.1) * mm});
            skPoint(sketch, "E2.12.30.0", {"position": v(12.7, -139.7) * mm});
            skPoint(sketch, "E2.12.31.0", {"position": v(12.7, -114.3) * mm});
            skPoint(sketch, "E2.12.32.0", {"position": v(12.7, -88.9) * mm});
            skPoint(sketch, "E2.12.33.0", {"position": v(12.7, -63.5) * mm});
            skPoint(sketch, "E2.12.34.0", {"position": v(12.7, -38.1) * mm});
            skPoint(sketch, "E2.12.35.0", {"position": v(12.7, -12.7) * mm});
            skPoint(sketch, "E2.12.36.0", {"position": v(12.7, 12.7) * mm});
            skPoint(sketch, "E2.12.37.0", {"position": v(12.7, 38.1) * mm});
            skPoint(sketch, "E2.12.38.0", {"position": v(12.7, 63.5) * mm});
            skPoint(sketch, "E2.12.39.0", {"position": v(12.7, 88.9) * mm});
            skPoint(sketch, "E2.12.40.0", {"position": v(12.7, 114.3) * mm});
            skPoint(sketch, "E2.12.41.0", {"position": v(12.7, 139.7) * mm});
            skPoint(sketch, "E2.12.42.0", {"position": v(12.7, 165.1) * mm});
            skPoint(sketch, "E2.12.43.0", {"position": v(12.7, 190.5) * mm});
            skPoint(sketch, "E2.12.44.0", {"position": v(12.7, 215.9) * mm});
            skPoint(sketch, "E2.12.45.0", {"position": v(12.7, 241.3) * mm});
            skPoint(sketch, "E2.12.46.0", {"position": v(12.7, 266.7) * mm});
            skPoint(sketch, "E2.12.47.0", {"position": v(12.7, 292.1) * mm});
            skPoint(sketch, "E2.12.48.0", {"position": v(12.7, 317.5) * mm});
            skPoint(sketch, "E2.12.49.0", {"position": v(12.7, 342.9) * mm});
            skPoint(sketch, "E2.12.50.0", {"position": v(12.7, 368.3) * mm});
            skPoint(sketch, "E2.12.51.0", {"position": v(12.7, 393.7) * mm});
            skPoint(sketch, "E2.12.52.0", {"position": v(12.7, 419.1) * mm});
            skPoint(sketch, "E2.12.53.0", {"position": v(12.7, 444.5) * mm});
            skPoint(sketch, "E2.12.54.0", {"position": v(12.7, 469.9) * mm});
            skPoint(sketch, "E2.12.55.0", {"position": v(12.7, 495.3) * mm});
            skPoint(sketch, "E2.12.56.0", {"position": v(12.7, 520.7) * mm});
            skPoint(sketch, "E2.12.57.0", {"position": v(12.7, 546.1) * mm});
            skPoint(sketch, "E2.12.58.0", {"position": v(12.7, 571.5) * mm});
            skPoint(sketch, "E2.12.59.0", {"position": v(12.7, 596.9) * mm});
            skPoint(sketch, "E2.12.60.0", {"position": v(12.7, 622.3) * mm});
            skPoint(sketch, "E2.12.61.0", {"position": v(12.7, 647.7) * mm});
            skPoint(sketch, "E2.12.62.0", {"position": v(12.7, 673.1) * mm});
            skPoint(sketch, "E2.12.63.0", {"position": v(12.7, 698.5) * mm});
            skPoint(sketch, "E2.12.64.0", {"position": v(12.7, 723.9) * mm});
            skPoint(sketch, "E2.12.65.0", {"position": v(12.7, 749.3) * mm});
            skPoint(sketch, "E2.12.66.0", {"position": v(12.7, 774.7) * mm});
            skPoint(sketch, "E2.12.67.0", {"position": v(12.7, 800.1) * mm});
            skPoint(sketch, "E2.12.68.0", {"position": v(12.7, 825.5) * mm});
            skPoint(sketch, "E2.12.69.0", {"position": v(12.7, 850.9) * mm});
            skPoint(sketch, "E2.12.70.0", {"position": v(12.7, 876.3) * mm});
            skPoint(sketch, "E2.12.71.0", {"position": v(12.7, 901.7) * mm});
            skPoint(sketch, "E2.13.0.0", {"position": v(38.1, -901.7) * mm});
            skPoint(sketch, "E2.13.1.0", {"position": v(38.1, -876.3) * mm});
            skPoint(sketch, "E2.13.2.0", {"position": v(38.1, -850.9) * mm});
            skPoint(sketch, "E2.13.3.0", {"position": v(38.1, -825.5) * mm});
            skPoint(sketch, "E2.13.4.0", {"position": v(38.1, -800.1) * mm});
            skPoint(sketch, "E2.13.5.0", {"position": v(38.1, -774.7) * mm});
            skPoint(sketch, "E2.13.6.0", {"position": v(38.1, -749.3) * mm});
            skPoint(sketch, "E2.13.7.0", {"position": v(38.1, -723.9) * mm});
            skPoint(sketch, "E2.13.8.0", {"position": v(38.1, -698.5) * mm});
            skPoint(sketch, "E2.13.9.0", {"position": v(38.1, -673.1) * mm});
            skPoint(sketch, "E2.13.10.0", {"position": v(38.1, -647.7) * mm});
            skPoint(sketch, "E2.13.11.0", {"position": v(38.1, -622.3) * mm});
            skPoint(sketch, "E2.13.12.0", {"position": v(38.1, -596.9) * mm});
            skPoint(sketch, "E2.13.13.0", {"position": v(38.1, -571.5) * mm});
            skPoint(sketch, "E2.13.14.0", {"position": v(38.1, -546.1) * mm});
            skPoint(sketch, "E2.13.15.0", {"position": v(38.1, -520.7) * mm});
            skPoint(sketch, "E2.13.16.0", {"position": v(38.1, -495.3) * mm});
            skPoint(sketch, "E2.13.17.0", {"position": v(38.1, -469.9) * mm});
            skPoint(sketch, "E2.13.18.0", {"position": v(38.1, -444.5) * mm});
            skPoint(sketch, "E2.13.19.0", {"position": v(38.1, -419.1) * mm});
            skPoint(sketch, "E2.13.20.0", {"position": v(38.1, -393.7) * mm});
            skPoint(sketch, "E2.13.21.0", {"position": v(38.1, -368.3) * mm});
            skPoint(sketch, "E2.13.22.0", {"position": v(38.1, -342.9) * mm});
            skPoint(sketch, "E2.13.23.0", {"position": v(38.1, -317.5) * mm});
            skPoint(sketch, "E2.13.24.0", {"position": v(38.1, -292.1) * mm});
            skPoint(sketch, "E2.13.25.0", {"position": v(38.1, -266.7) * mm});
            skPoint(sketch, "E2.13.26.0", {"position": v(38.1, -241.3) * mm});
            skPoint(sketch, "E2.13.27.0", {"position": v(38.1, -215.9) * mm});
            skPoint(sketch, "E2.13.28.0", {"position": v(38.1, -190.5) * mm});
            skPoint(sketch, "E2.13.29.0", {"position": v(38.1, -165.1) * mm});
            skPoint(sketch, "E2.13.30.0", {"position": v(38.1, -139.7) * mm});
            skPoint(sketch, "E2.13.31.0", {"position": v(38.1, -114.3) * mm});
            skPoint(sketch, "E2.13.32.0", {"position": v(38.1, -88.9) * mm});
            skPoint(sketch, "E2.13.33.0", {"position": v(38.1, -63.5) * mm});
            skPoint(sketch, "E2.13.34.0", {"position": v(38.1, -38.1) * mm});
            skPoint(sketch, "E2.13.35.0", {"position": v(38.1, -12.7) * mm});
            skPoint(sketch, "E2.13.36.0", {"position": v(38.1, 12.7) * mm});
            skPoint(sketch, "E2.13.37.0", {"position": v(38.1, 38.1) * mm});
            skPoint(sketch, "E2.13.38.0", {"position": v(38.1, 63.5) * mm});
            skPoint(sketch, "E2.13.39.0", {"position": v(38.1, 88.9) * mm});
            skPoint(sketch, "E2.13.40.0", {"position": v(38.1, 114.3) * mm});
            skPoint(sketch, "E2.13.41.0", {"position": v(38.1, 139.7) * mm});
            skPoint(sketch, "E2.13.42.0", {"position": v(38.1, 165.1) * mm});
            skPoint(sketch, "E2.13.43.0", {"position": v(38.1, 190.5) * mm});
            skPoint(sketch, "E2.13.44.0", {"position": v(38.1, 215.9) * mm});
            skPoint(sketch, "E2.13.45.0", {"position": v(38.1, 241.3) * mm});
            skPoint(sketch, "E2.13.46.0", {"position": v(38.1, 266.7) * mm});
            skPoint(sketch, "E2.13.47.0", {"position": v(38.1, 292.1) * mm});
            skPoint(sketch, "E2.13.48.0", {"position": v(38.1, 317.5) * mm});
            skPoint(sketch, "E2.13.49.0", {"position": v(38.1, 342.9) * mm});
            skPoint(sketch, "E2.13.50.0", {"position": v(38.1, 368.3) * mm});
            skPoint(sketch, "E2.13.51.0", {"position": v(38.1, 393.7) * mm});
            skPoint(sketch, "E2.13.52.0", {"position": v(38.1, 419.1) * mm});
            skPoint(sketch, "E2.13.53.0", {"position": v(38.1, 444.5) * mm});
            skPoint(sketch, "E2.13.54.0", {"position": v(38.1, 469.9) * mm});
            skPoint(sketch, "E2.13.55.0", {"position": v(38.1, 495.3) * mm});
            skPoint(sketch, "E2.13.56.0", {"position": v(38.1, 520.7) * mm});
            skPoint(sketch, "E2.13.57.0", {"position": v(38.1, 546.1) * mm});
            skPoint(sketch, "E2.13.58.0", {"position": v(38.1, 571.5) * mm});
            skPoint(sketch, "E2.13.59.0", {"position": v(38.1, 596.9) * mm});
            skPoint(sketch, "E2.13.60.0", {"position": v(38.1, 622.3) * mm});
            skPoint(sketch, "E2.13.61.0", {"position": v(38.1, 647.7) * mm});
            skPoint(sketch, "E2.13.62.0", {"position": v(38.1, 673.1) * mm});
            skPoint(sketch, "E2.13.63.0", {"position": v(38.1, 698.5) * mm});
            skPoint(sketch, "E2.13.64.0", {"position": v(38.1, 723.9) * mm});
            skPoint(sketch, "E2.13.65.0", {"position": v(38.1, 749.3) * mm});
            skPoint(sketch, "E2.13.66.0", {"position": v(38.1, 774.7) * mm});
            skPoint(sketch, "E2.13.67.0", {"position": v(38.1, 800.1) * mm});
            skPoint(sketch, "E2.13.68.0", {"position": v(38.1, 825.5) * mm});
            skPoint(sketch, "E2.13.69.0", {"position": v(38.1, 850.9) * mm});
            skPoint(sketch, "E2.13.70.0", {"position": v(38.1, 876.3) * mm});
            skPoint(sketch, "E2.13.71.0", {"position": v(38.1, 901.7) * mm});
            skPoint(sketch, "E2.14.0.0", {"position": v(63.5, -901.7) * mm});
            skPoint(sketch, "E2.14.1.0", {"position": v(63.5, -876.3) * mm});
            skPoint(sketch, "E2.14.2.0", {"position": v(63.5, -850.9) * mm});
            skPoint(sketch, "E2.14.3.0", {"position": v(63.5, -825.5) * mm});
            skPoint(sketch, "E2.14.4.0", {"position": v(63.5, -800.1) * mm});
            skPoint(sketch, "E2.14.5.0", {"position": v(63.5, -774.7) * mm});
            skPoint(sketch, "E2.14.6.0", {"position": v(63.5, -749.3) * mm});
            skPoint(sketch, "E2.14.7.0", {"position": v(63.5, -723.9) * mm});
            skPoint(sketch, "E2.14.8.0", {"position": v(63.5, -698.5) * mm});
            skPoint(sketch, "E2.14.9.0", {"position": v(63.5, -673.1) * mm});
            skPoint(sketch, "E2.14.10.0", {"position": v(63.5, -647.7) * mm});
            skPoint(sketch, "E2.14.11.0", {"position": v(63.5, -622.3) * mm});
            skPoint(sketch, "E2.14.12.0", {"position": v(63.5, -596.9) * mm});
            skPoint(sketch, "E2.14.13.0", {"position": v(63.5, -571.5) * mm});
            skPoint(sketch, "E2.14.14.0", {"position": v(63.5, -546.1) * mm});
            skPoint(sketch, "E2.14.15.0", {"position": v(63.5, -520.7) * mm});
            skPoint(sketch, "E2.14.16.0", {"position": v(63.5, -495.3) * mm});
            skPoint(sketch, "E2.14.17.0", {"position": v(63.5, -469.9) * mm});
            skPoint(sketch, "E2.14.18.0", {"position": v(63.5, -444.5) * mm});
            skPoint(sketch, "E2.14.19.0", {"position": v(63.5, -419.1) * mm});
            skPoint(sketch, "E2.14.20.0", {"position": v(63.5, -393.7) * mm});
            skPoint(sketch, "E2.14.21.0", {"position": v(63.5, -368.3) * mm});
            skPoint(sketch, "E2.14.22.0", {"position": v(63.5, -342.9) * mm});
            skPoint(sketch, "E2.14.23.0", {"position": v(63.5, -317.5) * mm});
            skPoint(sketch, "E2.14.24.0", {"position": v(63.5, -292.1) * mm});
            skPoint(sketch, "E2.14.25.0", {"position": v(63.5, -266.7) * mm});
            skPoint(sketch, "E2.14.26.0", {"position": v(63.5, -241.3) * mm});
            skPoint(sketch, "E2.14.27.0", {"position": v(63.5, -215.9) * mm});
            skPoint(sketch, "E2.14.28.0", {"position": v(63.5, -190.5) * mm});
            skPoint(sketch, "E2.14.29.0", {"position": v(63.5, -165.1) * mm});
            skPoint(sketch, "E2.14.30.0", {"position": v(63.5, -139.7) * mm});
            skPoint(sketch, "E2.14.31.0", {"position": v(63.5, -114.3) * mm});
            skPoint(sketch, "E2.14.32.0", {"position": v(63.5, -88.9) * mm});
            skPoint(sketch, "E2.14.33.0", {"position": v(63.5, -63.5) * mm});
            skPoint(sketch, "E2.14.34.0", {"position": v(63.5, -38.1) * mm});
            skPoint(sketch, "E2.14.35.0", {"position": v(63.5, -12.7) * mm});
            skPoint(sketch, "E2.14.36.0", {"position": v(63.5, 12.7) * mm});
            skPoint(sketch, "E2.14.37.0", {"position": v(63.5, 38.1) * mm});
            skPoint(sketch, "E2.14.38.0", {"position": v(63.5, 63.5) * mm});
            skPoint(sketch, "E2.14.39.0", {"position": v(63.5, 88.9) * mm});
            skPoint(sketch, "E2.14.40.0", {"position": v(63.5, 114.3) * mm});
            skPoint(sketch, "E2.14.41.0", {"position": v(63.5, 139.7) * mm});
            skPoint(sketch, "E2.14.42.0", {"position": v(63.5, 165.1) * mm});
            skPoint(sketch, "E2.14.43.0", {"position": v(63.5, 190.5) * mm});
            skPoint(sketch, "E2.14.44.0", {"position": v(63.5, 215.9) * mm});
            skPoint(sketch, "E2.14.45.0", {"position": v(63.5, 241.3) * mm});
            skPoint(sketch, "E2.14.46.0", {"position": v(63.5, 266.7) * mm});
            skPoint(sketch, "E2.14.47.0", {"position": v(63.5, 292.1) * mm});
            skPoint(sketch, "E2.14.48.0", {"position": v(63.5, 317.5) * mm});
            skPoint(sketch, "E2.14.49.0", {"position": v(63.5, 342.9) * mm});
            skPoint(sketch, "E2.14.50.0", {"position": v(63.5, 368.3) * mm});
            skPoint(sketch, "E2.14.51.0", {"position": v(63.5, 393.7) * mm});
            skPoint(sketch, "E2.14.52.0", {"position": v(63.5, 419.1) * mm});
            skPoint(sketch, "E2.14.53.0", {"position": v(63.5, 444.5) * mm});
            skPoint(sketch, "E2.14.54.0", {"position": v(63.5, 469.9) * mm});
            skPoint(sketch, "E2.14.55.0", {"position": v(63.5, 495.3) * mm});
            skPoint(sketch, "E2.14.56.0", {"position": v(63.5, 520.7) * mm});
            skPoint(sketch, "E2.14.57.0", {"position": v(63.5, 546.1) * mm});
            skPoint(sketch, "E2.14.58.0", {"position": v(63.5, 571.5) * mm});
            skPoint(sketch, "E2.14.59.0", {"position": v(63.5, 596.9) * mm});
            skPoint(sketch, "E2.14.60.0", {"position": v(63.5, 622.3) * mm});
            skPoint(sketch, "E2.14.61.0", {"position": v(63.5, 647.7) * mm});
            skPoint(sketch, "E2.14.62.0", {"position": v(63.5, 673.1) * mm});
            skPoint(sketch, "E2.14.63.0", {"position": v(63.5, 698.5) * mm});
            skPoint(sketch, "E2.14.64.0", {"position": v(63.5, 723.9) * mm});
            skPoint(sketch, "E2.14.65.0", {"position": v(63.5, 749.3) * mm});
            skPoint(sketch, "E2.14.66.0", {"position": v(63.5, 774.7) * mm});
            skPoint(sketch, "E2.14.67.0", {"position": v(63.5, 800.1) * mm});
            skPoint(sketch, "E2.14.68.0", {"position": v(63.5, 825.5) * mm});
            skPoint(sketch, "E2.14.69.0", {"position": v(63.5, 850.9) * mm});
            skPoint(sketch, "E2.14.70.0", {"position": v(63.5, 876.3) * mm});
            skPoint(sketch, "E2.14.71.0", {"position": v(63.5, 901.7) * mm});
            skPoint(sketch, "E2.15.0.0", {"position": v(88.9, -901.7) * mm});
            skPoint(sketch, "E2.15.1.0", {"position": v(88.9, -876.3) * mm});
            skPoint(sketch, "E2.15.2.0", {"position": v(88.9, -850.9) * mm});
            skPoint(sketch, "E2.15.3.0", {"position": v(88.9, -825.5) * mm});
            skPoint(sketch, "E2.15.4.0", {"position": v(88.9, -800.1) * mm});
            skPoint(sketch, "E2.15.5.0", {"position": v(88.9, -774.7) * mm});
            skPoint(sketch, "E2.15.6.0", {"position": v(88.9, -749.3) * mm});
            skPoint(sketch, "E2.15.7.0", {"position": v(88.9, -723.9) * mm});
            skPoint(sketch, "E2.15.8.0", {"position": v(88.9, -698.5) * mm});
            skPoint(sketch, "E2.15.9.0", {"position": v(88.9, -673.1) * mm});
            skPoint(sketch, "E2.15.10.0", {"position": v(88.9, -647.7) * mm});
            skPoint(sketch, "E2.15.11.0", {"position": v(88.9, -622.3) * mm});
            skPoint(sketch, "E2.15.12.0", {"position": v(88.9, -596.9) * mm});
            skPoint(sketch, "E2.15.13.0", {"position": v(88.9, -571.5) * mm});
            skPoint(sketch, "E2.15.14.0", {"position": v(88.9, -546.1) * mm});
            skPoint(sketch, "E2.15.15.0", {"position": v(88.9, -520.7) * mm});
            skPoint(sketch, "E2.15.16.0", {"position": v(88.9, -495.3) * mm});
            skPoint(sketch, "E2.15.17.0", {"position": v(88.9, -469.9) * mm});
            skPoint(sketch, "E2.15.18.0", {"position": v(88.9, -444.5) * mm});
            skPoint(sketch, "E2.15.19.0", {"position": v(88.9, -419.1) * mm});
            skPoint(sketch, "E2.15.20.0", {"position": v(88.9, -393.7) * mm});
            skPoint(sketch, "E2.15.21.0", {"position": v(88.9, -368.3) * mm});
            skPoint(sketch, "E2.15.22.0", {"position": v(88.9, -342.9) * mm});
            skPoint(sketch, "E2.15.23.0", {"position": v(88.9, -317.5) * mm});
            skPoint(sketch, "E2.15.24.0", {"position": v(88.9, -292.1) * mm});
            skPoint(sketch, "E2.15.25.0", {"position": v(88.9, -266.7) * mm});
            skPoint(sketch, "E2.15.26.0", {"position": v(88.9, -241.3) * mm});
            skPoint(sketch, "E2.15.27.0", {"position": v(88.9, -215.9) * mm});
            skPoint(sketch, "E2.15.28.0", {"position": v(88.9, -190.5) * mm});
            skPoint(sketch, "E2.15.29.0", {"position": v(88.9, -165.1) * mm});
            skPoint(sketch, "E2.15.30.0", {"position": v(88.9, -139.7) * mm});
            skPoint(sketch, "E2.15.31.0", {"position": v(88.9, -114.3) * mm});
            skPoint(sketch, "E2.15.32.0", {"position": v(88.9, -88.9) * mm});
            skPoint(sketch, "E2.15.33.0", {"position": v(88.9, -63.5) * mm});
            skPoint(sketch, "E2.15.34.0", {"position": v(88.9, -38.1) * mm});
            skPoint(sketch, "E2.15.35.0", {"position": v(88.9, -12.7) * mm});
            skPoint(sketch, "E2.15.36.0", {"position": v(88.9, 12.7) * mm});
            skPoint(sketch, "E2.15.37.0", {"position": v(88.9, 38.1) * mm});
            skPoint(sketch, "E2.15.38.0", {"position": v(88.9, 63.5) * mm});
            skPoint(sketch, "E2.15.39.0", {"position": v(88.9, 88.9) * mm});
            skPoint(sketch, "E2.15.40.0", {"position": v(88.9, 114.3) * mm});
            skPoint(sketch, "E2.15.41.0", {"position": v(88.9, 139.7) * mm});
            skPoint(sketch, "E2.15.42.0", {"position": v(88.9, 165.1) * mm});
            skPoint(sketch, "E2.15.43.0", {"position": v(88.9, 190.5) * mm});
            skPoint(sketch, "E2.15.44.0", {"position": v(88.9, 215.9) * mm});
            skPoint(sketch, "E2.15.45.0", {"position": v(88.9, 241.3) * mm});
            skPoint(sketch, "E2.15.46.0", {"position": v(88.9, 266.7) * mm});
            skPoint(sketch, "E2.15.47.0", {"position": v(88.9, 292.1) * mm});
            skPoint(sketch, "E2.15.48.0", {"position": v(88.9, 317.5) * mm});
            skPoint(sketch, "E2.15.49.0", {"position": v(88.9, 342.9) * mm});
            skPoint(sketch, "E2.15.50.0", {"position": v(88.9, 368.3) * mm});
            skPoint(sketch, "E2.15.51.0", {"position": v(88.9, 393.7) * mm});
            skPoint(sketch, "E2.15.52.0", {"position": v(88.9, 419.1) * mm});
            skPoint(sketch, "E2.15.53.0", {"position": v(88.9, 444.5) * mm});
            skPoint(sketch, "E2.15.54.0", {"position": v(88.9, 469.9) * mm});
            skPoint(sketch, "E2.15.55.0", {"position": v(88.9, 495.3) * mm});
            skPoint(sketch, "E2.15.56.0", {"position": v(88.9, 520.7) * mm});
            skPoint(sketch, "E2.15.57.0", {"position": v(88.9, 546.1) * mm});
            skPoint(sketch, "E2.15.58.0", {"position": v(88.9, 571.5) * mm});
            skPoint(sketch, "E2.15.59.0", {"position": v(88.9, 596.9) * mm});
            skPoint(sketch, "E2.15.60.0", {"position": v(88.9, 622.3) * mm});
            skPoint(sketch, "E2.15.61.0", {"position": v(88.9, 647.7) * mm});
            skPoint(sketch, "E2.15.62.0", {"position": v(88.9, 673.1) * mm});
            skPoint(sketch, "E2.15.63.0", {"position": v(88.9, 698.5) * mm});
            skPoint(sketch, "E2.15.64.0", {"position": v(88.9, 723.9) * mm});
            skPoint(sketch, "E2.15.65.0", {"position": v(88.9, 749.3) * mm});
            skPoint(sketch, "E2.15.66.0", {"position": v(88.9, 774.7) * mm});
            skPoint(sketch, "E2.15.67.0", {"position": v(88.9, 800.1) * mm});
            skPoint(sketch, "E2.15.68.0", {"position": v(88.9, 825.5) * mm});
            skPoint(sketch, "E2.15.69.0", {"position": v(88.9, 850.9) * mm});
            skPoint(sketch, "E2.15.70.0", {"position": v(88.9, 876.3) * mm});
            skPoint(sketch, "E2.15.71.0", {"position": v(88.9, 901.7) * mm});
            skPoint(sketch, "E2.16.0.0", {"position": v(114.3, -901.7) * mm});
            skPoint(sketch, "E2.16.1.0", {"position": v(114.3, -876.3) * mm});
            skPoint(sketch, "E2.16.2.0", {"position": v(114.3, -850.9) * mm});
            skPoint(sketch, "E2.16.3.0", {"position": v(114.3, -825.5) * mm});
            skPoint(sketch, "E2.16.4.0", {"position": v(114.3, -800.1) * mm});
            skPoint(sketch, "E2.16.5.0", {"position": v(114.3, -774.7) * mm});
            skPoint(sketch, "E2.16.6.0", {"position": v(114.3, -749.3) * mm});
            skPoint(sketch, "E2.16.7.0", {"position": v(114.3, -723.9) * mm});
            skPoint(sketch, "E2.16.8.0", {"position": v(114.3, -698.5) * mm});
            skPoint(sketch, "E2.16.9.0", {"position": v(114.3, -673.1) * mm});
            skPoint(sketch, "E2.16.10.0", {"position": v(114.3, -647.7) * mm});
            skPoint(sketch, "E2.16.11.0", {"position": v(114.3, -622.3) * mm});
            skPoint(sketch, "E2.16.12.0", {"position": v(114.3, -596.9) * mm});
            skPoint(sketch, "E2.16.13.0", {"position": v(114.3, -571.5) * mm});
            skPoint(sketch, "E2.16.14.0", {"position": v(114.3, -546.1) * mm});
            skPoint(sketch, "E2.16.15.0", {"position": v(114.3, -520.7) * mm});
            skPoint(sketch, "E2.16.16.0", {"position": v(114.3, -495.3) * mm});
            skPoint(sketch, "E2.16.17.0", {"position": v(114.3, -469.9) * mm});
            skPoint(sketch, "E2.16.18.0", {"position": v(114.3, -444.5) * mm});
            skPoint(sketch, "E2.16.19.0", {"position": v(114.3, -419.1) * mm});
            skPoint(sketch, "E2.16.20.0", {"position": v(114.3, -393.7) * mm});
            skPoint(sketch, "E2.16.21.0", {"position": v(114.3, -368.3) * mm});
            skPoint(sketch, "E2.16.22.0", {"position": v(114.3, -342.9) * mm});
            skPoint(sketch, "E2.16.23.0", {"position": v(114.3, -317.5) * mm});
            skPoint(sketch, "E2.16.24.0", {"position": v(114.3, -292.1) * mm});
            skPoint(sketch, "E2.16.25.0", {"position": v(114.3, -266.7) * mm});
            skPoint(sketch, "E2.16.26.0", {"position": v(114.3, -241.3) * mm});
            skPoint(sketch, "E2.16.27.0", {"position": v(114.3, -215.9) * mm});
            skPoint(sketch, "E2.16.28.0", {"position": v(114.3, -190.5) * mm});
            skPoint(sketch, "E2.16.29.0", {"position": v(114.3, -165.1) * mm});
            skPoint(sketch, "E2.16.30.0", {"position": v(114.3, -139.7) * mm});
            skPoint(sketch, "E2.16.31.0", {"position": v(114.3, -114.3) * mm});
            skPoint(sketch, "E2.16.32.0", {"position": v(114.3, -88.9) * mm});
            skPoint(sketch, "E2.16.33.0", {"position": v(114.3, -63.5) * mm});
            skPoint(sketch, "E2.16.34.0", {"position": v(114.3, -38.1) * mm});
            skPoint(sketch, "E2.16.35.0", {"position": v(114.3, -12.7) * mm});
            skPoint(sketch, "E2.16.36.0", {"position": v(114.3, 12.7) * mm});
            skPoint(sketch, "E2.16.37.0", {"position": v(114.3, 38.1) * mm});
            skPoint(sketch, "E2.16.38.0", {"position": v(114.3, 63.5) * mm});
            skPoint(sketch, "E2.16.39.0", {"position": v(114.3, 88.9) * mm});
            skPoint(sketch, "E2.16.40.0", {"position": v(114.3, 114.3) * mm});
            skPoint(sketch, "E2.16.41.0", {"position": v(114.3, 139.7) * mm});
            skPoint(sketch, "E2.16.42.0", {"position": v(114.3, 165.1) * mm});
            skPoint(sketch, "E2.16.43.0", {"position": v(114.3, 190.5) * mm});
            skPoint(sketch, "E2.16.44.0", {"position": v(114.3, 215.9) * mm});
            skPoint(sketch, "E2.16.45.0", {"position": v(114.3, 241.3) * mm});
            skPoint(sketch, "E2.16.46.0", {"position": v(114.3, 266.7) * mm});
            skPoint(sketch, "E2.16.47.0", {"position": v(114.3, 292.1) * mm});
            skPoint(sketch, "E2.16.48.0", {"position": v(114.3, 317.5) * mm});
            skPoint(sketch, "E2.16.49.0", {"position": v(114.3, 342.9) * mm});
            skPoint(sketch, "E2.16.50.0", {"position": v(114.3, 368.3) * mm});
            skPoint(sketch, "E2.16.51.0", {"position": v(114.3, 393.7) * mm});
            skPoint(sketch, "E2.16.52.0", {"position": v(114.3, 419.1) * mm});
            skPoint(sketch, "E2.16.53.0", {"position": v(114.3, 444.5) * mm});
            skPoint(sketch, "E2.16.54.0", {"position": v(114.3, 469.9) * mm});
            skPoint(sketch, "E2.16.55.0", {"position": v(114.3, 495.3) * mm});
            skPoint(sketch, "E2.16.56.0", {"position": v(114.3, 520.7) * mm});
            skPoint(sketch, "E2.16.57.0", {"position": v(114.3, 546.1) * mm});
            skPoint(sketch, "E2.16.58.0", {"position": v(114.3, 571.5) * mm});
            skPoint(sketch, "E2.16.59.0", {"position": v(114.3, 596.9) * mm});
            skPoint(sketch, "E2.16.60.0", {"position": v(114.3, 622.3) * mm});
            skPoint(sketch, "E2.16.61.0", {"position": v(114.3, 647.7) * mm});
            skPoint(sketch, "E2.16.62.0", {"position": v(114.3, 673.1) * mm});
            skPoint(sketch, "E2.16.63.0", {"position": v(114.3, 698.5) * mm});
            skPoint(sketch, "E2.16.64.0", {"position": v(114.3, 723.9) * mm});
            skPoint(sketch, "E2.16.65.0", {"position": v(114.3, 749.3) * mm});
            skPoint(sketch, "E2.16.66.0", {"position": v(114.3, 774.7) * mm});
            skPoint(sketch, "E2.16.67.0", {"position": v(114.3, 800.1) * mm});
            skPoint(sketch, "E2.16.68.0", {"position": v(114.3, 825.5) * mm});
            skPoint(sketch, "E2.16.69.0", {"position": v(114.3, 850.9) * mm});
            skPoint(sketch, "E2.16.70.0", {"position": v(114.3, 876.3) * mm});
            skPoint(sketch, "E2.16.71.0", {"position": v(114.3, 901.7) * mm});
            skPoint(sketch, "E2.17.0.0", {"position": v(139.7, -901.7) * mm});
            skPoint(sketch, "E2.17.1.0", {"position": v(139.7, -876.3) * mm});
            skPoint(sketch, "E2.17.2.0", {"position": v(139.7, -850.9) * mm});
            skPoint(sketch, "E2.17.3.0", {"position": v(139.7, -825.5) * mm});
            skPoint(sketch, "E2.17.4.0", {"position": v(139.7, -800.1) * mm});
            skPoint(sketch, "E2.17.5.0", {"position": v(139.7, -774.7) * mm});
            skPoint(sketch, "E2.17.6.0", {"position": v(139.7, -749.3) * mm});
            skPoint(sketch, "E2.17.7.0", {"position": v(139.7, -723.9) * mm});
            skPoint(sketch, "E2.17.8.0", {"position": v(139.7, -698.5) * mm});
            skPoint(sketch, "E2.17.9.0", {"position": v(139.7, -673.1) * mm});
            skPoint(sketch, "E2.17.10.0", {"position": v(139.7, -647.7) * mm});
            skPoint(sketch, "E2.17.11.0", {"position": v(139.7, -622.3) * mm});
            skPoint(sketch, "E2.17.12.0", {"position": v(139.7, -596.9) * mm});
            skPoint(sketch, "E2.17.13.0", {"position": v(139.7, -571.5) * mm});
            skPoint(sketch, "E2.17.14.0", {"position": v(139.7, -546.1) * mm});
            skPoint(sketch, "E2.17.15.0", {"position": v(139.7, -520.7) * mm});
            skPoint(sketch, "E2.17.16.0", {"position": v(139.7, -495.3) * mm});
            skPoint(sketch, "E2.17.17.0", {"position": v(139.7, -469.9) * mm});
            skPoint(sketch, "E2.17.18.0", {"position": v(139.7, -444.5) * mm});
            skPoint(sketch, "E2.17.19.0", {"position": v(139.7, -419.1) * mm});
            skPoint(sketch, "E2.17.20.0", {"position": v(139.7, -393.7) * mm});
            skPoint(sketch, "E2.17.21.0", {"position": v(139.7, -368.3) * mm});
            skPoint(sketch, "E2.17.22.0", {"position": v(139.7, -342.9) * mm});
            skPoint(sketch, "E2.17.23.0", {"position": v(139.7, -317.5) * mm});
            skPoint(sketch, "E2.17.24.0", {"position": v(139.7, -292.1) * mm});
            skPoint(sketch, "E2.17.25.0", {"position": v(139.7, -266.7) * mm});
            skPoint(sketch, "E2.17.26.0", {"position": v(139.7, -241.3) * mm});
            skPoint(sketch, "E2.17.27.0", {"position": v(139.7, -215.9) * mm});
            skPoint(sketch, "E2.17.28.0", {"position": v(139.7, -190.5) * mm});
            skPoint(sketch, "E2.17.29.0", {"position": v(139.7, -165.1) * mm});
            skPoint(sketch, "E2.17.30.0", {"position": v(139.7, -139.7) * mm});
            skPoint(sketch, "E2.17.31.0", {"position": v(139.7, -114.3) * mm});
            skPoint(sketch, "E2.17.32.0", {"position": v(139.7, -88.9) * mm});
            skPoint(sketch, "E2.17.33.0", {"position": v(139.7, -63.5) * mm});
            skPoint(sketch, "E2.17.34.0", {"position": v(139.7, -38.1) * mm});
            skPoint(sketch, "E2.17.35.0", {"position": v(139.7, -12.7) * mm});
            skPoint(sketch, "E2.17.36.0", {"position": v(139.7, 12.7) * mm});
            skPoint(sketch, "E2.17.37.0", {"position": v(139.7, 38.1) * mm});
            skPoint(sketch, "E2.17.38.0", {"position": v(139.7, 63.5) * mm});
            skPoint(sketch, "E2.17.39.0", {"position": v(139.7, 88.9) * mm});
            skPoint(sketch, "E2.17.40.0", {"position": v(139.7, 114.3) * mm});
            skPoint(sketch, "E2.17.41.0", {"position": v(139.7, 139.7) * mm});
            skPoint(sketch, "E2.17.42.0", {"position": v(139.7, 165.1) * mm});
            skPoint(sketch, "E2.17.43.0", {"position": v(139.7, 190.5) * mm});
            skPoint(sketch, "E2.17.44.0", {"position": v(139.7, 215.9) * mm});
            skPoint(sketch, "E2.17.45.0", {"position": v(139.7, 241.3) * mm});
            skPoint(sketch, "E2.17.46.0", {"position": v(139.7, 266.7) * mm});
            skPoint(sketch, "E2.17.47.0", {"position": v(139.7, 292.1) * mm});
            skPoint(sketch, "E2.17.48.0", {"position": v(139.7, 317.5) * mm});
            skPoint(sketch, "E2.17.49.0", {"position": v(139.7, 342.9) * mm});
            skPoint(sketch, "E2.17.50.0", {"position": v(139.7, 368.3) * mm});
            skPoint(sketch, "E2.17.51.0", {"position": v(139.7, 393.7) * mm});
            skPoint(sketch, "E2.17.52.0", {"position": v(139.7, 419.1) * mm});
            skPoint(sketch, "E2.17.53.0", {"position": v(139.7, 444.5) * mm});
            skPoint(sketch, "E2.17.54.0", {"position": v(139.7, 469.9) * mm});
            skPoint(sketch, "E2.17.55.0", {"position": v(139.7, 495.3) * mm});
            skPoint(sketch, "E2.17.56.0", {"position": v(139.7, 520.7) * mm});
            skPoint(sketch, "E2.17.57.0", {"position": v(139.7, 546.1) * mm});
            skPoint(sketch, "E2.17.58.0", {"position": v(139.7, 571.5) * mm});
            skPoint(sketch, "E2.17.59.0", {"position": v(139.7, 596.9) * mm});
            skPoint(sketch, "E2.17.60.0", {"position": v(139.7, 622.3) * mm});
            skPoint(sketch, "E2.17.61.0", {"position": v(139.7, 647.7) * mm});
            skPoint(sketch, "E2.17.62.0", {"position": v(139.7, 673.1) * mm});
            skPoint(sketch, "E2.17.63.0", {"position": v(139.7, 698.5) * mm});
            skPoint(sketch, "E2.17.64.0", {"position": v(139.7, 723.9) * mm});
            skPoint(sketch, "E2.17.65.0", {"position": v(139.7, 749.3) * mm});
            skPoint(sketch, "E2.17.66.0", {"position": v(139.7, 774.7) * mm});
            skPoint(sketch, "E2.17.67.0", {"position": v(139.7, 800.1) * mm});
            skPoint(sketch, "E2.17.68.0", {"position": v(139.7, 825.5) * mm});
            skPoint(sketch, "E2.17.69.0", {"position": v(139.7, 850.9) * mm});
            skPoint(sketch, "E2.17.70.0", {"position": v(139.7, 876.3) * mm});
            skPoint(sketch, "E2.17.71.0", {"position": v(139.7, 901.7) * mm});
            skPoint(sketch, "E2.18.0.0", {"position": v(165.1, -901.7) * mm});
            skPoint(sketch, "E2.18.1.0", {"position": v(165.1, -876.3) * mm});
            skPoint(sketch, "E2.18.2.0", {"position": v(165.1, -850.9) * mm});
            skPoint(sketch, "E2.18.3.0", {"position": v(165.1, -825.5) * mm});
            skPoint(sketch, "E2.18.4.0", {"position": v(165.1, -800.1) * mm});
            skPoint(sketch, "E2.18.5.0", {"position": v(165.1, -774.7) * mm});
            skPoint(sketch, "E2.18.6.0", {"position": v(165.1, -749.3) * mm});
            skPoint(sketch, "E2.18.7.0", {"position": v(165.1, -723.9) * mm});
            skPoint(sketch, "E2.18.8.0", {"position": v(165.1, -698.5) * mm});
            skPoint(sketch, "E2.18.9.0", {"position": v(165.1, -673.1) * mm});
            skPoint(sketch, "E2.18.10.0", {"position": v(165.1, -647.7) * mm});
            skPoint(sketch, "E2.18.11.0", {"position": v(165.1, -622.3) * mm});
            skPoint(sketch, "E2.18.12.0", {"position": v(165.1, -596.9) * mm});
            skPoint(sketch, "E2.18.13.0", {"position": v(165.1, -571.5) * mm});
            skPoint(sketch, "E2.18.14.0", {"position": v(165.1, -546.1) * mm});
            skPoint(sketch, "E2.18.15.0", {"position": v(165.1, -520.7) * mm});
            skPoint(sketch, "E2.18.16.0", {"position": v(165.1, -495.3) * mm});
            skPoint(sketch, "E2.18.17.0", {"position": v(165.1, -469.9) * mm});
            skPoint(sketch, "E2.18.18.0", {"position": v(165.1, -444.5) * mm});
            skPoint(sketch, "E2.18.19.0", {"position": v(165.1, -419.1) * mm});
            skPoint(sketch, "E2.18.20.0", {"position": v(165.1, -393.7) * mm});
            skPoint(sketch, "E2.18.21.0", {"position": v(165.1, -368.3) * mm});
            skPoint(sketch, "E2.18.22.0", {"position": v(165.1, -342.9) * mm});
            skPoint(sketch, "E2.18.23.0", {"position": v(165.1, -317.5) * mm});
            skPoint(sketch, "E2.18.24.0", {"position": v(165.1, -292.1) * mm});
            skPoint(sketch, "E2.18.25.0", {"position": v(165.1, -266.7) * mm});
            skPoint(sketch, "E2.18.26.0", {"position": v(165.1, -241.3) * mm});
            skPoint(sketch, "E2.18.27.0", {"position": v(165.1, -215.9) * mm});
            skPoint(sketch, "E2.18.28.0", {"position": v(165.1, -190.5) * mm});
            skPoint(sketch, "E2.18.29.0", {"position": v(165.1, -165.1) * mm});
            skPoint(sketch, "E2.18.30.0", {"position": v(165.1, -139.7) * mm});
            skPoint(sketch, "E2.18.31.0", {"position": v(165.1, -114.3) * mm});
            skPoint(sketch, "E2.18.32.0", {"position": v(165.1, -88.9) * mm});
            skPoint(sketch, "E2.18.33.0", {"position": v(165.1, -63.5) * mm});
            skPoint(sketch, "E2.18.34.0", {"position": v(165.1, -38.1) * mm});
            skPoint(sketch, "E2.18.35.0", {"position": v(165.1, -12.7) * mm});
            skPoint(sketch, "E2.18.36.0", {"position": v(165.1, 12.7) * mm});
            skPoint(sketch, "E2.18.37.0", {"position": v(165.1, 38.1) * mm});
            skPoint(sketch, "E2.18.38.0", {"position": v(165.1, 63.5) * mm});
            skPoint(sketch, "E2.18.39.0", {"position": v(165.1, 88.9) * mm});
            skPoint(sketch, "E2.18.40.0", {"position": v(165.1, 114.3) * mm});
            skPoint(sketch, "E2.18.41.0", {"position": v(165.1, 139.7) * mm});
            skPoint(sketch, "E2.18.42.0", {"position": v(165.1, 165.1) * mm});
            skPoint(sketch, "E2.18.43.0", {"position": v(165.1, 190.5) * mm});
            skPoint(sketch, "E2.18.44.0", {"position": v(165.1, 215.9) * mm});
            skPoint(sketch, "E2.18.45.0", {"position": v(165.1, 241.3) * mm});
            skPoint(sketch, "E2.18.46.0", {"position": v(165.1, 266.7) * mm});
            skPoint(sketch, "E2.18.47.0", {"position": v(165.1, 292.1) * mm});
            skPoint(sketch, "E2.18.48.0", {"position": v(165.1, 317.5) * mm});
            skPoint(sketch, "E2.18.49.0", {"position": v(165.1, 342.9) * mm});
            skPoint(sketch, "E2.18.50.0", {"position": v(165.1, 368.3) * mm});
            skPoint(sketch, "E2.18.51.0", {"position": v(165.1, 393.7) * mm});
            skPoint(sketch, "E2.18.52.0", {"position": v(165.1, 419.1) * mm});
            skPoint(sketch, "E2.18.53.0", {"position": v(165.1, 444.5) * mm});
            skPoint(sketch, "E2.18.54.0", {"position": v(165.1, 469.9) * mm});
            skPoint(sketch, "E2.18.55.0", {"position": v(165.1, 495.3) * mm});
            skPoint(sketch, "E2.18.56.0", {"position": v(165.1, 520.7) * mm});
            skPoint(sketch, "E2.18.57.0", {"position": v(165.1, 546.1) * mm});
            skPoint(sketch, "E2.18.58.0", {"position": v(165.1, 571.5) * mm});
            skPoint(sketch, "E2.18.59.0", {"position": v(165.1, 596.9) * mm});
            skPoint(sketch, "E2.18.60.0", {"position": v(165.1, 622.3) * mm});
            skPoint(sketch, "E2.18.61.0", {"position": v(165.1, 647.7) * mm});
            skPoint(sketch, "E2.18.62.0", {"position": v(165.1, 673.1) * mm});
            skPoint(sketch, "E2.18.63.0", {"position": v(165.1, 698.5) * mm});
            skPoint(sketch, "E2.18.64.0", {"position": v(165.1, 723.9) * mm});
            skPoint(sketch, "E2.18.65.0", {"position": v(165.1, 749.3) * mm});
            skPoint(sketch, "E2.18.66.0", {"position": v(165.1, 774.7) * mm});
            skPoint(sketch, "E2.18.67.0", {"position": v(165.1, 800.1) * mm});
            skPoint(sketch, "E2.18.68.0", {"position": v(165.1, 825.5) * mm});
            skPoint(sketch, "E2.18.69.0", {"position": v(165.1, 850.9) * mm});
            skPoint(sketch, "E2.18.70.0", {"position": v(165.1, 876.3) * mm});
            skPoint(sketch, "E2.18.71.0", {"position": v(165.1, 901.7) * mm});
            skPoint(sketch, "E2.19.0.0", {"position": v(190.5, -901.7) * mm});
            skPoint(sketch, "E2.19.1.0", {"position": v(190.5, -876.3) * mm});
            skPoint(sketch, "E2.19.2.0", {"position": v(190.5, -850.9) * mm});
            skPoint(sketch, "E2.19.3.0", {"position": v(190.5, -825.5) * mm});
            skPoint(sketch, "E2.19.4.0", {"position": v(190.5, -800.1) * mm});
            skPoint(sketch, "E2.19.5.0", {"position": v(190.5, -774.7) * mm});
            skPoint(sketch, "E2.19.6.0", {"position": v(190.5, -749.3) * mm});
            skPoint(sketch, "E2.19.7.0", {"position": v(190.5, -723.9) * mm});
            skPoint(sketch, "E2.19.8.0", {"position": v(190.5, -698.5) * mm});
            skPoint(sketch, "E2.19.9.0", {"position": v(190.5, -673.1) * mm});
            skPoint(sketch, "E2.19.10.0", {"position": v(190.5, -647.7) * mm});
            skPoint(sketch, "E2.19.11.0", {"position": v(190.5, -622.3) * mm});
            skPoint(sketch, "E2.19.12.0", {"position": v(190.5, -596.9) * mm});
            skPoint(sketch, "E2.19.13.0", {"position": v(190.5, -571.5) * mm});
            skPoint(sketch, "E2.19.14.0", {"position": v(190.5, -546.1) * mm});
            skPoint(sketch, "E2.19.15.0", {"position": v(190.5, -520.7) * mm});
            skPoint(sketch, "E2.19.16.0", {"position": v(190.5, -495.3) * mm});
            skPoint(sketch, "E2.19.17.0", {"position": v(190.5, -469.9) * mm});
            skPoint(sketch, "E2.19.18.0", {"position": v(190.5, -444.5) * mm});
            skPoint(sketch, "E2.19.19.0", {"position": v(190.5, -419.1) * mm});
            skPoint(sketch, "E2.19.20.0", {"position": v(190.5, -393.7) * mm});
            skPoint(sketch, "E2.19.21.0", {"position": v(190.5, -368.3) * mm});
            skPoint(sketch, "E2.19.22.0", {"position": v(190.5, -342.9) * mm});
            skPoint(sketch, "E2.19.23.0", {"position": v(190.5, -317.5) * mm});
            skPoint(sketch, "E2.19.24.0", {"position": v(190.5, -292.1) * mm});
            skPoint(sketch, "E2.19.25.0", {"position": v(190.5, -266.7) * mm});
            skPoint(sketch, "E2.19.26.0", {"position": v(190.5, -241.3) * mm});
            skPoint(sketch, "E2.19.27.0", {"position": v(190.5, -215.9) * mm});
            skPoint(sketch, "E2.19.28.0", {"position": v(190.5, -190.5) * mm});
            skPoint(sketch, "E2.19.29.0", {"position": v(190.5, -165.1) * mm});
            skPoint(sketch, "E2.19.30.0", {"position": v(190.5, -139.7) * mm});
            skPoint(sketch, "E2.19.31.0", {"position": v(190.5, -114.3) * mm});
            skPoint(sketch, "E2.19.32.0", {"position": v(190.5, -88.9) * mm});
            skPoint(sketch, "E2.19.33.0", {"position": v(190.5, -63.5) * mm});
            skPoint(sketch, "E2.19.34.0", {"position": v(190.5, -38.1) * mm});
            skPoint(sketch, "E2.19.35.0", {"position": v(190.5, -12.7) * mm});
            skPoint(sketch, "E2.19.36.0", {"position": v(190.5, 12.7) * mm});
            skPoint(sketch, "E2.19.37.0", {"position": v(190.5, 38.1) * mm});
            skPoint(sketch, "E2.19.38.0", {"position": v(190.5, 63.5) * mm});
            skPoint(sketch, "E2.19.39.0", {"position": v(190.5, 88.9) * mm});
            skPoint(sketch, "E2.19.40.0", {"position": v(190.5, 114.3) * mm});
            skPoint(sketch, "E2.19.41.0", {"position": v(190.5, 139.7) * mm});
            skPoint(sketch, "E2.19.42.0", {"position": v(190.5, 165.1) * mm});
            skPoint(sketch, "E2.19.43.0", {"position": v(190.5, 190.5) * mm});
            skPoint(sketch, "E2.19.44.0", {"position": v(190.5, 215.9) * mm});
            skPoint(sketch, "E2.19.45.0", {"position": v(190.5, 241.3) * mm});
            skPoint(sketch, "E2.19.46.0", {"position": v(190.5, 266.7) * mm});
            skPoint(sketch, "E2.19.47.0", {"position": v(190.5, 292.1) * mm});
            skPoint(sketch, "E2.19.48.0", {"position": v(190.5, 317.5) * mm});
            skPoint(sketch, "E2.19.49.0", {"position": v(190.5, 342.9) * mm});
            skPoint(sketch, "E2.19.50.0", {"position": v(190.5, 368.3) * mm});
            skPoint(sketch, "E2.19.51.0", {"position": v(190.5, 393.7) * mm});
            skPoint(sketch, "E2.19.52.0", {"position": v(190.5, 419.1) * mm});
            skPoint(sketch, "E2.19.53.0", {"position": v(190.5, 444.5) * mm});
            skPoint(sketch, "E2.19.54.0", {"position": v(190.5, 469.9) * mm});
            skPoint(sketch, "E2.19.55.0", {"position": v(190.5, 495.3) * mm});
            skPoint(sketch, "E2.19.56.0", {"position": v(190.5, 520.7) * mm});
            skPoint(sketch, "E2.19.57.0", {"position": v(190.5, 546.1) * mm});
            skPoint(sketch, "E2.19.58.0", {"position": v(190.5, 571.5) * mm});
            skPoint(sketch, "E2.19.59.0", {"position": v(190.5, 596.9) * mm});
            skPoint(sketch, "E2.19.60.0", {"position": v(190.5, 622.3) * mm});
            skPoint(sketch, "E2.19.61.0", {"position": v(190.5, 647.7) * mm});
            skPoint(sketch, "E2.19.62.0", {"position": v(190.5, 673.1) * mm});
            skPoint(sketch, "E2.19.63.0", {"position": v(190.5, 698.5) * mm});
            skPoint(sketch, "E2.19.64.0", {"position": v(190.5, 723.9) * mm});
            skPoint(sketch, "E2.19.65.0", {"position": v(190.5, 749.3) * mm});
            skPoint(sketch, "E2.19.66.0", {"position": v(190.5, 774.7) * mm});
            skPoint(sketch, "E2.19.67.0", {"position": v(190.5, 800.1) * mm});
            skPoint(sketch, "E2.19.68.0", {"position": v(190.5, 825.5) * mm});
            skPoint(sketch, "E2.19.69.0", {"position": v(190.5, 850.9) * mm});
            skPoint(sketch, "E2.19.70.0", {"position": v(190.5, 876.3) * mm});
            skPoint(sketch, "E2.19.71.0", {"position": v(190.5, 901.7) * mm});
            skPoint(sketch, "E2.20.0.0", {"position": v(215.9, -901.7) * mm});
            skPoint(sketch, "E2.20.1.0", {"position": v(215.9, -876.3) * mm});
            skPoint(sketch, "E2.20.2.0", {"position": v(215.9, -850.9) * mm});
            skPoint(sketch, "E2.20.3.0", {"position": v(215.9, -825.5) * mm});
            skPoint(sketch, "E2.20.4.0", {"position": v(215.9, -800.1) * mm});
            skPoint(sketch, "E2.20.5.0", {"position": v(215.9, -774.7) * mm});
            skPoint(sketch, "E2.20.6.0", {"position": v(215.9, -749.3) * mm});
            skPoint(sketch, "E2.20.7.0", {"position": v(215.9, -723.9) * mm});
            skPoint(sketch, "E2.20.8.0", {"position": v(215.9, -698.5) * mm});
            skPoint(sketch, "E2.20.9.0", {"position": v(215.9, -673.1) * mm});
            skPoint(sketch, "E2.20.10.0", {"position": v(215.9, -647.7) * mm});
            skPoint(sketch, "E2.20.11.0", {"position": v(215.9, -622.3) * mm});
            skPoint(sketch, "E2.20.12.0", {"position": v(215.9, -596.9) * mm});
            skPoint(sketch, "E2.20.13.0", {"position": v(215.9, -571.5) * mm});
            skPoint(sketch, "E2.20.14.0", {"position": v(215.9, -546.1) * mm});
            skPoint(sketch, "E2.20.15.0", {"position": v(215.9, -520.7) * mm});
            skPoint(sketch, "E2.20.16.0", {"position": v(215.9, -495.3) * mm});
            skPoint(sketch, "E2.20.17.0", {"position": v(215.9, -469.9) * mm});
            skPoint(sketch, "E2.20.18.0", {"position": v(215.9, -444.5) * mm});
            skPoint(sketch, "E2.20.19.0", {"position": v(215.9, -419.1) * mm});
            skPoint(sketch, "E2.20.20.0", {"position": v(215.9, -393.7) * mm});
            skPoint(sketch, "E2.20.21.0", {"position": v(215.9, -368.3) * mm});
            skPoint(sketch, "E2.20.22.0", {"position": v(215.9, -342.9) * mm});
            skPoint(sketch, "E2.20.23.0", {"position": v(215.9, -317.5) * mm});
            skPoint(sketch, "E2.20.24.0", {"position": v(215.9, -292.1) * mm});
            skPoint(sketch, "E2.20.25.0", {"position": v(215.9, -266.7) * mm});
            skPoint(sketch, "E2.20.26.0", {"position": v(215.9, -241.3) * mm});
            skPoint(sketch, "E2.20.27.0", {"position": v(215.9, -215.9) * mm});
            skPoint(sketch, "E2.20.28.0", {"position": v(215.9, -190.5) * mm});
            skPoint(sketch, "E2.20.29.0", {"position": v(215.9, -165.1) * mm});
            skPoint(sketch, "E2.20.30.0", {"position": v(215.9, -139.7) * mm});
            skPoint(sketch, "E2.20.31.0", {"position": v(215.9, -114.3) * mm});
            skPoint(sketch, "E2.20.32.0", {"position": v(215.9, -88.9) * mm});
            skPoint(sketch, "E2.20.33.0", {"position": v(215.9, -63.5) * mm});
            skPoint(sketch, "E2.20.34.0", {"position": v(215.9, -38.1) * mm});
            skPoint(sketch, "E2.20.35.0", {"position": v(215.9, -12.7) * mm});
            skPoint(sketch, "E2.20.36.0", {"position": v(215.9, 12.7) * mm});
            skPoint(sketch, "E2.20.37.0", {"position": v(215.9, 38.1) * mm});
            skPoint(sketch, "E2.20.38.0", {"position": v(215.9, 63.5) * mm});
            skPoint(sketch, "E2.20.39.0", {"position": v(215.9, 88.9) * mm});
            skPoint(sketch, "E2.20.40.0", {"position": v(215.9, 114.3) * mm});
            skPoint(sketch, "E2.20.41.0", {"position": v(215.9, 139.7) * mm});
            skPoint(sketch, "E2.20.42.0", {"position": v(215.9, 165.1) * mm});
            skPoint(sketch, "E2.20.43.0", {"position": v(215.9, 190.5) * mm});
            skPoint(sketch, "E2.20.44.0", {"position": v(215.9, 215.9) * mm});
            skPoint(sketch, "E2.20.45.0", {"position": v(215.9, 241.3) * mm});
            skPoint(sketch, "E2.20.46.0", {"position": v(215.9, 266.7) * mm});
            skPoint(sketch, "E2.20.47.0", {"position": v(215.9, 292.1) * mm});
            skPoint(sketch, "E2.20.48.0", {"position": v(215.9, 317.5) * mm});
            skPoint(sketch, "E2.20.49.0", {"position": v(215.9, 342.9) * mm});
            skPoint(sketch, "E2.20.50.0", {"position": v(215.9, 368.3) * mm});
            skPoint(sketch, "E2.20.51.0", {"position": v(215.9, 393.7) * mm});
            skPoint(sketch, "E2.20.52.0", {"position": v(215.9, 419.1) * mm});
            skPoint(sketch, "E2.20.53.0", {"position": v(215.9, 444.5) * mm});
            skPoint(sketch, "E2.20.54.0", {"position": v(215.9, 469.9) * mm});
            skPoint(sketch, "E2.20.55.0", {"position": v(215.9, 495.3) * mm});
            skPoint(sketch, "E2.20.56.0", {"position": v(215.9, 520.7) * mm});
            skPoint(sketch, "E2.20.57.0", {"position": v(215.9, 546.1) * mm});
            skPoint(sketch, "E2.20.58.0", {"position": v(215.9, 571.5) * mm});
            skPoint(sketch, "E2.20.59.0", {"position": v(215.9, 596.9) * mm});
            skPoint(sketch, "E2.20.60.0", {"position": v(215.9, 622.3) * mm});
            skPoint(sketch, "E2.20.61.0", {"position": v(215.9, 647.7) * mm});
            skPoint(sketch, "E2.20.62.0", {"position": v(215.9, 673.1) * mm});
            skPoint(sketch, "E2.20.63.0", {"position": v(215.9, 698.5) * mm});
            skPoint(sketch, "E2.20.64.0", {"position": v(215.9, 723.9) * mm});
            skPoint(sketch, "E2.20.65.0", {"position": v(215.9, 749.3) * mm});
            skPoint(sketch, "E2.20.66.0", {"position": v(215.9, 774.7) * mm});
            skPoint(sketch, "E2.20.67.0", {"position": v(215.9, 800.1) * mm});
            skPoint(sketch, "E2.20.68.0", {"position": v(215.9, 825.5) * mm});
            skPoint(sketch, "E2.20.69.0", {"position": v(215.9, 850.9) * mm});
            skPoint(sketch, "E2.20.70.0", {"position": v(215.9, 876.3) * mm});
            skPoint(sketch, "E2.20.71.0", {"position": v(215.9, 901.7) * mm});
            skPoint(sketch, "E2.21.0.0", {"position": v(241.3, -901.7) * mm});
            skPoint(sketch, "E2.21.1.0", {"position": v(241.3, -876.3) * mm});
            skPoint(sketch, "E2.21.2.0", {"position": v(241.3, -850.9) * mm});
            skPoint(sketch, "E2.21.3.0", {"position": v(241.3, -825.5) * mm});
            skPoint(sketch, "E2.21.4.0", {"position": v(241.3, -800.1) * mm});
            skPoint(sketch, "E2.21.5.0", {"position": v(241.3, -774.7) * mm});
            skPoint(sketch, "E2.21.6.0", {"position": v(241.3, -749.3) * mm});
            skPoint(sketch, "E2.21.7.0", {"position": v(241.3, -723.9) * mm});
            skPoint(sketch, "E2.21.8.0", {"position": v(241.3, -698.5) * mm});
            skPoint(sketch, "E2.21.9.0", {"position": v(241.3, -673.1) * mm});
            skPoint(sketch, "E2.21.10.0", {"position": v(241.3, -647.7) * mm});
            skPoint(sketch, "E2.21.11.0", {"position": v(241.3, -622.3) * mm});
            skPoint(sketch, "E2.21.12.0", {"position": v(241.3, -596.9) * mm});
            skPoint(sketch, "E2.21.13.0", {"position": v(241.3, -571.5) * mm});
            skPoint(sketch, "E2.21.14.0", {"position": v(241.3, -546.1) * mm});
            skPoint(sketch, "E2.21.15.0", {"position": v(241.3, -520.7) * mm});
            skPoint(sketch, "E2.21.16.0", {"position": v(241.3, -495.3) * mm});
            skPoint(sketch, "E2.21.17.0", {"position": v(241.3, -469.9) * mm});
            skPoint(sketch, "E2.21.18.0", {"position": v(241.3, -444.5) * mm});
            skPoint(sketch, "E2.21.19.0", {"position": v(241.3, -419.1) * mm});
            skPoint(sketch, "E2.21.20.0", {"position": v(241.3, -393.7) * mm});
            skPoint(sketch, "E2.21.21.0", {"position": v(241.3, -368.3) * mm});
            skPoint(sketch, "E2.21.22.0", {"position": v(241.3, -342.9) * mm});
            skPoint(sketch, "E2.21.23.0", {"position": v(241.3, -317.5) * mm});
            skPoint(sketch, "E2.21.24.0", {"position": v(241.3, -292.1) * mm});
            skPoint(sketch, "E2.21.25.0", {"position": v(241.3, -266.7) * mm});
            skPoint(sketch, "E2.21.26.0", {"position": v(241.3, -241.3) * mm});
            skPoint(sketch, "E2.21.27.0", {"position": v(241.3, -215.9) * mm});
            skPoint(sketch, "E2.21.28.0", {"position": v(241.3, -190.5) * mm});
            skPoint(sketch, "E2.21.29.0", {"position": v(241.3, -165.1) * mm});
            skPoint(sketch, "E2.21.30.0", {"position": v(241.3, -139.7) * mm});
            skPoint(sketch, "E2.21.31.0", {"position": v(241.3, -114.3) * mm});
            skPoint(sketch, "E2.21.32.0", {"position": v(241.3, -88.9) * mm});
            skPoint(sketch, "E2.21.33.0", {"position": v(241.3, -63.5) * mm});
            skPoint(sketch, "E2.21.34.0", {"position": v(241.3, -38.1) * mm});
            skPoint(sketch, "E2.21.35.0", {"position": v(241.3, -12.7) * mm});
            skPoint(sketch, "E2.21.36.0", {"position": v(241.3, 12.7) * mm});
            skPoint(sketch, "E2.21.37.0", {"position": v(241.3, 38.1) * mm});
            skPoint(sketch, "E2.21.38.0", {"position": v(241.3, 63.5) * mm});
            skPoint(sketch, "E2.21.39.0", {"position": v(241.3, 88.9) * mm});
            skPoint(sketch, "E2.21.40.0", {"position": v(241.3, 114.3) * mm});
            skPoint(sketch, "E2.21.41.0", {"position": v(241.3, 139.7) * mm});
            skPoint(sketch, "E2.21.42.0", {"position": v(241.3, 165.1) * mm});
            skPoint(sketch, "E2.21.43.0", {"position": v(241.3, 190.5) * mm});
            skPoint(sketch, "E2.21.44.0", {"position": v(241.3, 215.9) * mm});
            skPoint(sketch, "E2.21.45.0", {"position": v(241.3, 241.3) * mm});
            skPoint(sketch, "E2.21.46.0", {"position": v(241.3, 266.7) * mm});
            skPoint(sketch, "E2.21.47.0", {"position": v(241.3, 292.1) * mm});
            skPoint(sketch, "E2.21.48.0", {"position": v(241.3, 317.5) * mm});
            skPoint(sketch, "E2.21.49.0", {"position": v(241.3, 342.9) * mm});
            skPoint(sketch, "E2.21.50.0", {"position": v(241.3, 368.3) * mm});
            skPoint(sketch, "E2.21.51.0", {"position": v(241.3, 393.7) * mm});
            skPoint(sketch, "E2.21.52.0", {"position": v(241.3, 419.1) * mm});
            skPoint(sketch, "E2.21.53.0", {"position": v(241.3, 444.5) * mm});
            skPoint(sketch, "E2.21.54.0", {"position": v(241.3, 469.9) * mm});
            skPoint(sketch, "E2.21.55.0", {"position": v(241.3, 495.3) * mm});
            skPoint(sketch, "E2.21.56.0", {"position": v(241.3, 520.7) * mm});
            skPoint(sketch, "E2.21.57.0", {"position": v(241.3, 546.1) * mm});
            skPoint(sketch, "E2.21.58.0", {"position": v(241.3, 571.5) * mm});
            skPoint(sketch, "E2.21.59.0", {"position": v(241.3, 596.9) * mm});
            skPoint(sketch, "E2.21.60.0", {"position": v(241.3, 622.3) * mm});
            skPoint(sketch, "E2.21.61.0", {"position": v(241.3, 647.7) * mm});
            skPoint(sketch, "E2.21.62.0", {"position": v(241.3, 673.1) * mm});
            skPoint(sketch, "E2.21.63.0", {"position": v(241.3, 698.5) * mm});
            skPoint(sketch, "E2.21.64.0", {"position": v(241.3, 723.9) * mm});
            skPoint(sketch, "E2.21.65.0", {"position": v(241.3, 749.3) * mm});
            skPoint(sketch, "E2.21.66.0", {"position": v(241.3, 774.7) * mm});
            skPoint(sketch, "E2.21.67.0", {"position": v(241.3, 800.1) * mm});
            skPoint(sketch, "E2.21.68.0", {"position": v(241.3, 825.5) * mm});
            skPoint(sketch, "E2.21.69.0", {"position": v(241.3, 850.9) * mm});
            skPoint(sketch, "E2.21.70.0", {"position": v(241.3, 876.3) * mm});
            skPoint(sketch, "E2.21.71.0", {"position": v(241.3, 901.7) * mm});
            skPoint(sketch, "E2.22.0.0", {"position": v(266.7, -901.7) * mm});
            skPoint(sketch, "E2.22.1.0", {"position": v(266.7, -876.3) * mm});
            skPoint(sketch, "E2.22.2.0", {"position": v(266.7, -850.9) * mm});
            skPoint(sketch, "E2.22.3.0", {"position": v(266.7, -825.5) * mm});
            skPoint(sketch, "E2.22.4.0", {"position": v(266.7, -800.1) * mm});
            skPoint(sketch, "E2.22.5.0", {"position": v(266.7, -774.7) * mm});
            skPoint(sketch, "E2.22.6.0", {"position": v(266.7, -749.3) * mm});
            skPoint(sketch, "E2.22.7.0", {"position": v(266.7, -723.9) * mm});
            skPoint(sketch, "E2.22.8.0", {"position": v(266.7, -698.5) * mm});
            skPoint(sketch, "E2.22.9.0", {"position": v(266.7, -673.1) * mm});
            skPoint(sketch, "E2.22.10.0", {"position": v(266.7, -647.7) * mm});
            skPoint(sketch, "E2.22.11.0", {"position": v(266.7, -622.3) * mm});
            skPoint(sketch, "E2.22.12.0", {"position": v(266.7, -596.9) * mm});
            skPoint(sketch, "E2.22.13.0", {"position": v(266.7, -571.5) * mm});
            skPoint(sketch, "E2.22.14.0", {"position": v(266.7, -546.1) * mm});
            skPoint(sketch, "E2.22.15.0", {"position": v(266.7, -520.7) * mm});
            skPoint(sketch, "E2.22.16.0", {"position": v(266.7, -495.3) * mm});
            skPoint(sketch, "E2.22.17.0", {"position": v(266.7, -469.9) * mm});
            skPoint(sketch, "E2.22.18.0", {"position": v(266.7, -444.5) * mm});
            skPoint(sketch, "E2.22.19.0", {"position": v(266.7, -419.1) * mm});
            skPoint(sketch, "E2.22.20.0", {"position": v(266.7, -393.7) * mm});
            skPoint(sketch, "E2.22.21.0", {"position": v(266.7, -368.3) * mm});
            skPoint(sketch, "E2.22.22.0", {"position": v(266.7, -342.9) * mm});
            skPoint(sketch, "E2.22.23.0", {"position": v(266.7, -317.5) * mm});
            skPoint(sketch, "E2.22.24.0", {"position": v(266.7, -292.1) * mm});
            skPoint(sketch, "E2.22.25.0", {"position": v(266.7, -266.7) * mm});
            skPoint(sketch, "E2.22.26.0", {"position": v(266.7, -241.3) * mm});
            skPoint(sketch, "E2.22.27.0", {"position": v(266.7, -215.9) * mm});
            skPoint(sketch, "E2.22.28.0", {"position": v(266.7, -190.5) * mm});
            skPoint(sketch, "E2.22.29.0", {"position": v(266.7, -165.1) * mm});
            skPoint(sketch, "E2.22.30.0", {"position": v(266.7, -139.7) * mm});
            skPoint(sketch, "E2.22.31.0", {"position": v(266.7, -114.3) * mm});
            skPoint(sketch, "E2.22.32.0", {"position": v(266.7, -88.9) * mm});
            skPoint(sketch, "E2.22.33.0", {"position": v(266.7, -63.5) * mm});
            skPoint(sketch, "E2.22.34.0", {"position": v(266.7, -38.1) * mm});
            skPoint(sketch, "E2.22.35.0", {"position": v(266.7, -12.7) * mm});
            skPoint(sketch, "E2.22.36.0", {"position": v(266.7, 12.7) * mm});
            skPoint(sketch, "E2.22.37.0", {"position": v(266.7, 38.1) * mm});
            skPoint(sketch, "E2.22.38.0", {"position": v(266.7, 63.5) * mm});
            skPoint(sketch, "E2.22.39.0", {"position": v(266.7, 88.9) * mm});
            skPoint(sketch, "E2.22.40.0", {"position": v(266.7, 114.3) * mm});
            skPoint(sketch, "E2.22.41.0", {"position": v(266.7, 139.7) * mm});
            skPoint(sketch, "E2.22.42.0", {"position": v(266.7, 165.1) * mm});
            skPoint(sketch, "E2.22.43.0", {"position": v(266.7, 190.5) * mm});
            skPoint(sketch, "E2.22.44.0", {"position": v(266.7, 215.9) * mm});
            skPoint(sketch, "E2.22.45.0", {"position": v(266.7, 241.3) * mm});
            skPoint(sketch, "E2.22.46.0", {"position": v(266.7, 266.7) * mm});
            skPoint(sketch, "E2.22.47.0", {"position": v(266.7, 292.1) * mm});
            skPoint(sketch, "E2.22.48.0", {"position": v(266.7, 317.5) * mm});
            skPoint(sketch, "E2.22.49.0", {"position": v(266.7, 342.9) * mm});
            skPoint(sketch, "E2.22.50.0", {"position": v(266.7, 368.3) * mm});
            skPoint(sketch, "E2.22.51.0", {"position": v(266.7, 393.7) * mm});
            skPoint(sketch, "E2.22.52.0", {"position": v(266.7, 419.1) * mm});
            skPoint(sketch, "E2.22.53.0", {"position": v(266.7, 444.5) * mm});
            skPoint(sketch, "E2.22.54.0", {"position": v(266.7, 469.9) * mm});
            skPoint(sketch, "E2.22.55.0", {"position": v(266.7, 495.3) * mm});
            skPoint(sketch, "E2.22.56.0", {"position": v(266.7, 520.7) * mm});
            skPoint(sketch, "E2.22.57.0", {"position": v(266.7, 546.1) * mm});
            skPoint(sketch, "E2.22.58.0", {"position": v(266.7, 571.5) * mm});
            skPoint(sketch, "E2.22.59.0", {"position": v(266.7, 596.9) * mm});
            skPoint(sketch, "E2.22.60.0", {"position": v(266.7, 622.3) * mm});
            skPoint(sketch, "E2.22.61.0", {"position": v(266.7, 647.7) * mm});
            skPoint(sketch, "E2.22.62.0", {"position": v(266.7, 673.1) * mm});
            skPoint(sketch, "E2.22.63.0", {"position": v(266.7, 698.5) * mm});
            skPoint(sketch, "E2.22.64.0", {"position": v(266.7, 723.9) * mm});
            skPoint(sketch, "E2.22.65.0", {"position": v(266.7, 749.3) * mm});
            skPoint(sketch, "E2.22.66.0", {"position": v(266.7, 774.7) * mm});
            skPoint(sketch, "E2.22.67.0", {"position": v(266.7, 800.1) * mm});
            skPoint(sketch, "E2.22.68.0", {"position": v(266.7, 825.5) * mm});
            skPoint(sketch, "E2.22.69.0", {"position": v(266.7, 850.9) * mm});
            skPoint(sketch, "E2.22.70.0", {"position": v(266.7, 876.3) * mm});
            skPoint(sketch, "E2.22.71.0", {"position": v(266.7, 901.7) * mm});
            skPoint(sketch, "E2.23.0.0", {"position": v(292.1, -901.7) * mm});
            skPoint(sketch, "E2.23.1.0", {"position": v(292.1, -876.3) * mm});
            skPoint(sketch, "E2.23.2.0", {"position": v(292.1, -850.9) * mm});
            skPoint(sketch, "E2.23.3.0", {"position": v(292.1, -825.5) * mm});
            skPoint(sketch, "E2.23.4.0", {"position": v(292.1, -800.1) * mm});
            skPoint(sketch, "E2.23.5.0", {"position": v(292.1, -774.7) * mm});
            skPoint(sketch, "E2.23.6.0", {"position": v(292.1, -749.3) * mm});
            skPoint(sketch, "E2.23.7.0", {"position": v(292.1, -723.9) * mm});
            skPoint(sketch, "E2.23.8.0", {"position": v(292.1, -698.5) * mm});
            skPoint(sketch, "E2.23.9.0", {"position": v(292.1, -673.1) * mm});
            skPoint(sketch, "E2.23.10.0", {"position": v(292.1, -647.7) * mm});
            skPoint(sketch, "E2.23.11.0", {"position": v(292.1, -622.3) * mm});
            skPoint(sketch, "E2.23.12.0", {"position": v(292.1, -596.9) * mm});
            skPoint(sketch, "E2.23.13.0", {"position": v(292.1, -571.5) * mm});
            skPoint(sketch, "E2.23.14.0", {"position": v(292.1, -546.1) * mm});
            skPoint(sketch, "E2.23.15.0", {"position": v(292.1, -520.7) * mm});
            skPoint(sketch, "E2.23.16.0", {"position": v(292.1, -495.3) * mm});
            skPoint(sketch, "E2.23.17.0", {"position": v(292.1, -469.9) * mm});
            skPoint(sketch, "E2.23.18.0", {"position": v(292.1, -444.5) * mm});
            skPoint(sketch, "E2.23.19.0", {"position": v(292.1, -419.1) * mm});
            skPoint(sketch, "E2.23.20.0", {"position": v(292.1, -393.7) * mm});
            skPoint(sketch, "E2.23.21.0", {"position": v(292.1, -368.3) * mm});
            skPoint(sketch, "E2.23.22.0", {"position": v(292.1, -342.9) * mm});
            skPoint(sketch, "E2.23.23.0", {"position": v(292.1, -317.5) * mm});
            skPoint(sketch, "E2.23.24.0", {"position": v(292.1, -292.1) * mm});
            skPoint(sketch, "E2.23.25.0", {"position": v(292.1, -266.7) * mm});
            skPoint(sketch, "E2.23.26.0", {"position": v(292.1, -241.3) * mm});
            skPoint(sketch, "E2.23.27.0", {"position": v(292.1, -215.9) * mm});
            skPoint(sketch, "E2.23.28.0", {"position": v(292.1, -190.5) * mm});
            skPoint(sketch, "E2.23.29.0", {"position": v(292.1, -165.1) * mm});
            skPoint(sketch, "E2.23.30.0", {"position": v(292.1, -139.7) * mm});
            skPoint(sketch, "E2.23.31.0", {"position": v(292.1, -114.3) * mm});
            skPoint(sketch, "E2.23.32.0", {"position": v(292.1, -88.9) * mm});
            skPoint(sketch, "E2.23.33.0", {"position": v(292.1, -63.5) * mm});
            skPoint(sketch, "E2.23.34.0", {"position": v(292.1, -38.1) * mm});
            skPoint(sketch, "E2.23.35.0", {"position": v(292.1, -12.7) * mm});
            skPoint(sketch, "E2.23.36.0", {"position": v(292.1, 12.7) * mm});
            skPoint(sketch, "E2.23.37.0", {"position": v(292.1, 38.1) * mm});
            skPoint(sketch, "E2.23.38.0", {"position": v(292.1, 63.5) * mm});
            skPoint(sketch, "E2.23.39.0", {"position": v(292.1, 88.9) * mm});
            skPoint(sketch, "E2.23.40.0", {"position": v(292.1, 114.3) * mm});
            skPoint(sketch, "E2.23.41.0", {"position": v(292.1, 139.7) * mm});
            skPoint(sketch, "E2.23.42.0", {"position": v(292.1, 165.1) * mm});
            skPoint(sketch, "E2.23.43.0", {"position": v(292.1, 190.5) * mm});
            skPoint(sketch, "E2.23.44.0", {"position": v(292.1, 215.9) * mm});
            skPoint(sketch, "E2.23.45.0", {"position": v(292.1, 241.3) * mm});
            skPoint(sketch, "E2.23.46.0", {"position": v(292.1, 266.7) * mm});
            skPoint(sketch, "E2.23.47.0", {"position": v(292.1, 292.1) * mm});
            skPoint(sketch, "E2.23.48.0", {"position": v(292.1, 317.5) * mm});
            skPoint(sketch, "E2.23.49.0", {"position": v(292.1, 342.9) * mm});
            skPoint(sketch, "E2.23.50.0", {"position": v(292.1, 368.3) * mm});
            skPoint(sketch, "E2.23.51.0", {"position": v(292.1, 393.7) * mm});
            skPoint(sketch, "E2.23.52.0", {"position": v(292.1, 419.1) * mm});
            skPoint(sketch, "E2.23.53.0", {"position": v(292.1, 444.5) * mm});
            skPoint(sketch, "E2.23.54.0", {"position": v(292.1, 469.9) * mm});
            skPoint(sketch, "E2.23.55.0", {"position": v(292.1, 495.3) * mm});
            skPoint(sketch, "E2.23.56.0", {"position": v(292.1, 520.7) * mm});
            skPoint(sketch, "E2.23.57.0", {"position": v(292.1, 546.1) * mm});
            skPoint(sketch, "E2.23.58.0", {"position": v(292.1, 571.5) * mm});
            skPoint(sketch, "E2.23.59.0", {"position": v(292.1, 596.9) * mm});
            skPoint(sketch, "E2.23.60.0", {"position": v(292.1, 622.3) * mm});
            skPoint(sketch, "E2.23.61.0", {"position": v(292.1, 647.7) * mm});
            skPoint(sketch, "E2.23.62.0", {"position": v(292.1, 673.1) * mm});
            skPoint(sketch, "E2.23.63.0", {"position": v(292.1, 698.5) * mm});
            skPoint(sketch, "E2.23.64.0", {"position": v(292.1, 723.9) * mm});
            skPoint(sketch, "E2.23.65.0", {"position": v(292.1, 749.3) * mm});
            skPoint(sketch, "E2.23.66.0", {"position": v(292.1, 774.7) * mm});
            skPoint(sketch, "E2.23.67.0", {"position": v(292.1, 800.1) * mm});
            skPoint(sketch, "E2.23.68.0", {"position": v(292.1, 825.5) * mm});
            skPoint(sketch, "E2.23.69.0", {"position": v(292.1, 850.9) * mm});
            skPoint(sketch, "E2.23.70.0", {"position": v(292.1, 876.3) * mm});
            skPoint(sketch, "E2.23.71.0", {"position": v(292.1, 901.7) * mm});
            skLineSegment(sketch, "E2.direction1", {"start": v(-292.1, -901.7) * mm, "end": v(-266.7, -901.7) * mm, "construction": true});
            skLineSegment(sketch, "E2.direction2", {"start": v(-292.1, -901.7) * mm, "end": v(-292.1, -876.3) * mm, "construction": true});
            skSolve(sketch);
        }
        {
            var Q0;
            Q0 = qSketchRegion(id + "F0", true);
            extrude(context, id + "F1", {"entities" : qUnion([Q0]), "depth" : 6.35 * mm});
        }
        {
            var Q0;
            Q0=sQuery(id+"F0.wireOp",VERTEX,"E1");
            var Q1;
            Q1=sQuery(id+"F0.wireOp",VERTEX,"E2.1.0.0");
            var Q2;
            Q2=sQuery(id+"F0.wireOp",VERTEX,"E2.2.0.0");
            var Q3;
            Q3=sQuery(id+"F0.wireOp",VERTEX,"E2.3.0.0");
            var Q4;
            Q4=sQuery(id+"F0.wireOp",VERTEX,"E2.4.0.0");
            var Q5;
            Q5=sQuery(id+"F0.wireOp",VERTEX,"E2.5.0.0");
            var Q6;
            Q6=sQuery(id+"F0.wireOp",VERTEX,"E2.6.0.0");
            var Q7;
            Q7=sQuery(id+"F0.wireOp",VERTEX,"E2.7.0.0");
            var Q8;
            Q8=sQuery(id+"F0.wireOp",VERTEX,"E2.8.0.0");
            var Q9;
            Q9=sQuery(id+"F0.wireOp",VERTEX,"E2.9.0.0");
            var Q10;
            Q10=sQuery(id+"F0.wireOp",VERTEX,"E2.10.0.0");
            var Q11;
            Q11=sQuery(id+"F0.wireOp",VERTEX,"E2.11.0.0");
            var Q12;
            Q12=sQuery(id+"F0.wireOp",VERTEX,"E2.12.0.0");
            var Q13;
            Q13=sQuery(id+"F0.wireOp",VERTEX,"E2.13.0.0");
            var Q14;
            Q14=sQuery(id+"F0.wireOp",VERTEX,"E2.14.0.0");
            var Q15;
            Q15=sQuery(id+"F0.wireOp",VERTEX,"E2.16.0.0");
            var Q16;
            Q16=sQuery(id+"F0.wireOp",VERTEX,"E2.18.0.0");
            var Q17;
            Q17=sQuery(id+"F0.wireOp",VERTEX,"E2.19.0.0");
            var Q18;
            Q18=sQuery(id+"F0.wireOp",VERTEX,"E2.20.0.0");
            var Q19;
            Q19=sQuery(id+"F0.wireOp",VERTEX,"E2.21.0.0");
            var Q20;
            Q20=sQuery(id+"F0.wireOp",VERTEX,"E2.22.0.0");
            var Q21;
            Q21=sQuery(id+"F0.wireOp",VERTEX,"E2.23.0.0");
            var Q22;
            Q22=sQuery(id+"F0.wireOp",VERTEX,"E2.17.0.0");
            var Q23;
            Q23=sQuery(id+"F0.wireOp",VERTEX,"E2.15.0.0");
            var Q24;
            Q24=sQuery(id+"F0.wireOp",VERTEX,"E2.23.1.0");
            var Q25;
            Q25=sQuery(id+"F0.wireOp",VERTEX,"E2.23.2.0");
            var Q26;
            Q26=sQuery(id+"F0.wireOp",VERTEX,"E2.23.3.0");
            var Q27;
            Q27=sQuery(id+"F0.wireOp",VERTEX,"E2.23.4.0");
            var Q28;
            Q28=sQuery(id+"F0.wireOp",VERTEX,"E2.23.5.0");
            var Q29;
            Q29=sQuery(id+"F0.wireOp",VERTEX,"E2.23.7.0");
            var Q30;
            Q30=sQuery(id+"F0.wireOp",VERTEX,"E2.23.8.0");
            var Q31;
            Q31=sQuery(id+"F0.wireOp",VERTEX,"E2.23.6.0");
            var Q32;
            Q32=sQuery(id+"F0.wireOp",VERTEX,"E2.23.9.0");
            var Q33;
            Q33=sQuery(id+"F0.wireOp",VERTEX,"E2.23.10.0");
            var Q34;
            Q34=sQuery(id+"F0.wireOp",VERTEX,"E2.22.1.0");
            var Q35;
            Q35=sQuery(id+"F0.wireOp",VERTEX,"E2.21.1.0");
            var Q36;
            Q36=sQuery(id+"F0.wireOp",VERTEX,"E2.20.1.0");
            var Q37;
            Q37=sQuery(id+"F0.wireOp",VERTEX,"E2.19.1.0");
            var Q38;
            Q38=sQuery(id+"F0.wireOp",VERTEX,"E2.18.1.0");
            var Q39;
            Q39=sQuery(id+"F0.wireOp",VERTEX,"E2.20.1.0");
            var Q40;
            Q40=sQuery(id+"F0.wireOp",VERTEX,"E2.17.1.0");
            var Q41;
            Q41=sQuery(id+"F0.wireOp",VERTEX,"E2.16.1.0");
            var Q42;
            Q42=sQuery(id+"F0.wireOp",VERTEX,"E2.15.1.0");
            var Q43;
            Q43=sQuery(id+"F0.wireOp",VERTEX,"E2.14.1.0");
            var Q44;
            Q44=sQuery(id+"F0.wireOp",VERTEX,"E2.13.1.0");
            var Q45;
            Q45=sQuery(id+"F0.wireOp",VERTEX,"E2.12.1.0");
            var Q46;
            Q46=sQuery(id+"F0.wireOp",VERTEX,"E2.11.1.0");
            var Q47;
            Q47=sQuery(id+"F0.wireOp",VERTEX,"E2.10.1.0");
            var Q48;
            Q48=sQuery(id+"F0.wireOp",VERTEX,"E2.9.1.0");
            var Q49;
            Q49=sQuery(id+"F0.wireOp",VERTEX,"E2.8.1.0");
            var Q50;
            Q50=sQuery(id+"F0.wireOp",VERTEX,"E2.7.1.0");
            var Q51;
            Q51=sQuery(id+"F0.wireOp",VERTEX,"E2.6.1.0");
            var Q52;
            Q52=sQuery(id+"F0.wireOp",VERTEX,"E2.5.1.0");
            var Q53;
            Q53=sQuery(id+"F0.wireOp",VERTEX,"E2.4.1.0");
            var Q54;
            Q54=sQuery(id+"F0.wireOp",VERTEX,"E2.3.1.0");
            var Q55;
            Q55=sQuery(id+"F0.wireOp",VERTEX,"E2.2.1.0");
            var Q56;
            Q56=sQuery(id+"F0.wireOp",VERTEX,"E2.1.1.0");
            var Q57;
            Q57=sQuery(id+"F0.wireOp",VERTEX,"E2.0.1.0");
            var Q58;
            Q58=sQuery(id+"F0.wireOp",VERTEX,"E2.0.2.0");
            var Q59;
            Q59=sQuery(id+"F0.wireOp",VERTEX,"E2.1.2.0");
            var Q60;
            Q60=sQuery(id+"F0.wireOp",VERTEX,"E2.1.3.0");
            var Q61;
            Q61=sQuery(id+"F0.wireOp",VERTEX,"E2.0.3.0");
            var Q62;
            Q62=sQuery(id+"F0.wireOp",VERTEX,"E2.0.4.0");
            var Q63;
            Q63=sQuery(id+"F0.wireOp",VERTEX,"E2.1.4.0");
            var Q64;
            Q64=sQuery(id+"F0.wireOp",VERTEX,"E2.1.5.0");
            var Q65;
            Q65=sQuery(id+"F0.wireOp",VERTEX,"E2.0.5.0");
            var Q66;
            Q66=sQuery(id+"F0.wireOp",VERTEX,"E2.0.6.0");
            var Q67;
            Q67=sQuery(id+"F0.wireOp",VERTEX,"E2.1.6.0");
            var Q68;
            Q68=sQuery(id+"F0.wireOp",VERTEX,"E2.1.7.0");
            var Q69;
            Q69=sQuery(id+"F0.wireOp",VERTEX,"E2.0.7.0");
            var Q70;
            Q70=sQuery(id+"F0.wireOp",VERTEX,"E2.0.8.0");
            var Q71;
            Q71=sQuery(id+"F0.wireOp",VERTEX,"E2.1.8.0");
            var Q72;
            Q72=sQuery(id+"F0.wireOp",VERTEX,"E2.22.10.0");
            var Q73;
            Q73=sQuery(id+"F0.wireOp",VERTEX,"E2.22.9.0");
            var Q74;
            Q74=sQuery(id+"F0.wireOp",VERTEX,"E2.22.8.0");
            var Q75;
            Q75=sQuery(id+"F0.wireOp",VERTEX,"E2.22.6.0");
            var Q76;
            Q76=sQuery(id+"F0.wireOp",VERTEX,"E2.22.4.0");
            var Q77;
            Q77=sQuery(id+"F0.wireOp",VERTEX,"E2.22.3.0");
            var Q78;
            Q78=sQuery(id+"F0.wireOp",VERTEX,"E2.22.2.0");
            var Q79;
            Q79=sQuery(id+"F0.wireOp",VERTEX,"E2.0.71.0");
            var Q80;
            Q80=sQuery(id+"F0.wireOp",VERTEX,"E2.0.70.0");
            var Q81;
            Q81=sQuery(id+"F0.wireOp",VERTEX,"E2.1.71.0");
            var Q82;
            Q82=sQuery(id+"F0.wireOp",VERTEX,"E2.2.71.0");
            var Q83;
            Q83=sQuery(id+"F0.wireOp",VERTEX,"E2.3.71.0");
            var Q84;
            Q84=makeQuery(id+"F1.opExtrude","SWEPT_BODY",BODY,{"disambiguationData":[OSD([sQuery(id+"F0.wireOp",EDGE,"E0.bottom"),sQuery(id+"F0.wireOp",EDGE,"E0.top"),sQuery(id+"F0.wireOp",EDGE,"E0.left"),sQuery(id+"F0.wireOp",EDGE,"E0.right")])]});
            hole(context, id + "F2", {"style" : HoleStyle.SIMPLE, "endStyle" : HoleEndStyle.THROUGH, "oppositeDirection" : true, "holeDiameter" : 6.35 * mm, "locations" : qUnion([Q0, Q1, Q2, Q3, Q4, Q5, Q6, Q7, Q8, Q9, Q10, Q11, Q12, Q13, Q14, Q15, Q16, Q17, Q18, Q19, Q20, Q21, Q22, Q23, Q24, Q25, Q26, Q27, Q28, Q29, Q30, Q31, Q32, Q33, Q34, Q35, Q36, Q37, Q38, Q39, Q40, Q41, Q42, Q43, Q44, Q45, Q46, Q47, Q48, Q49, Q50, Q51, Q52, Q53, Q54, Q55, Q56, Q57, Q58, Q59, Q60, Q61, Q62, Q63, Q64, Q65, Q66, Q67, Q68, Q69, Q70, Q71, Q72, Q73, Q74, Q75, Q76, Q77, Q78, Q79, Q80, Q81, Q82, Q83]), "scope" : qUnion([Q84]), "isTappedThrough" : true});
        }
    });
